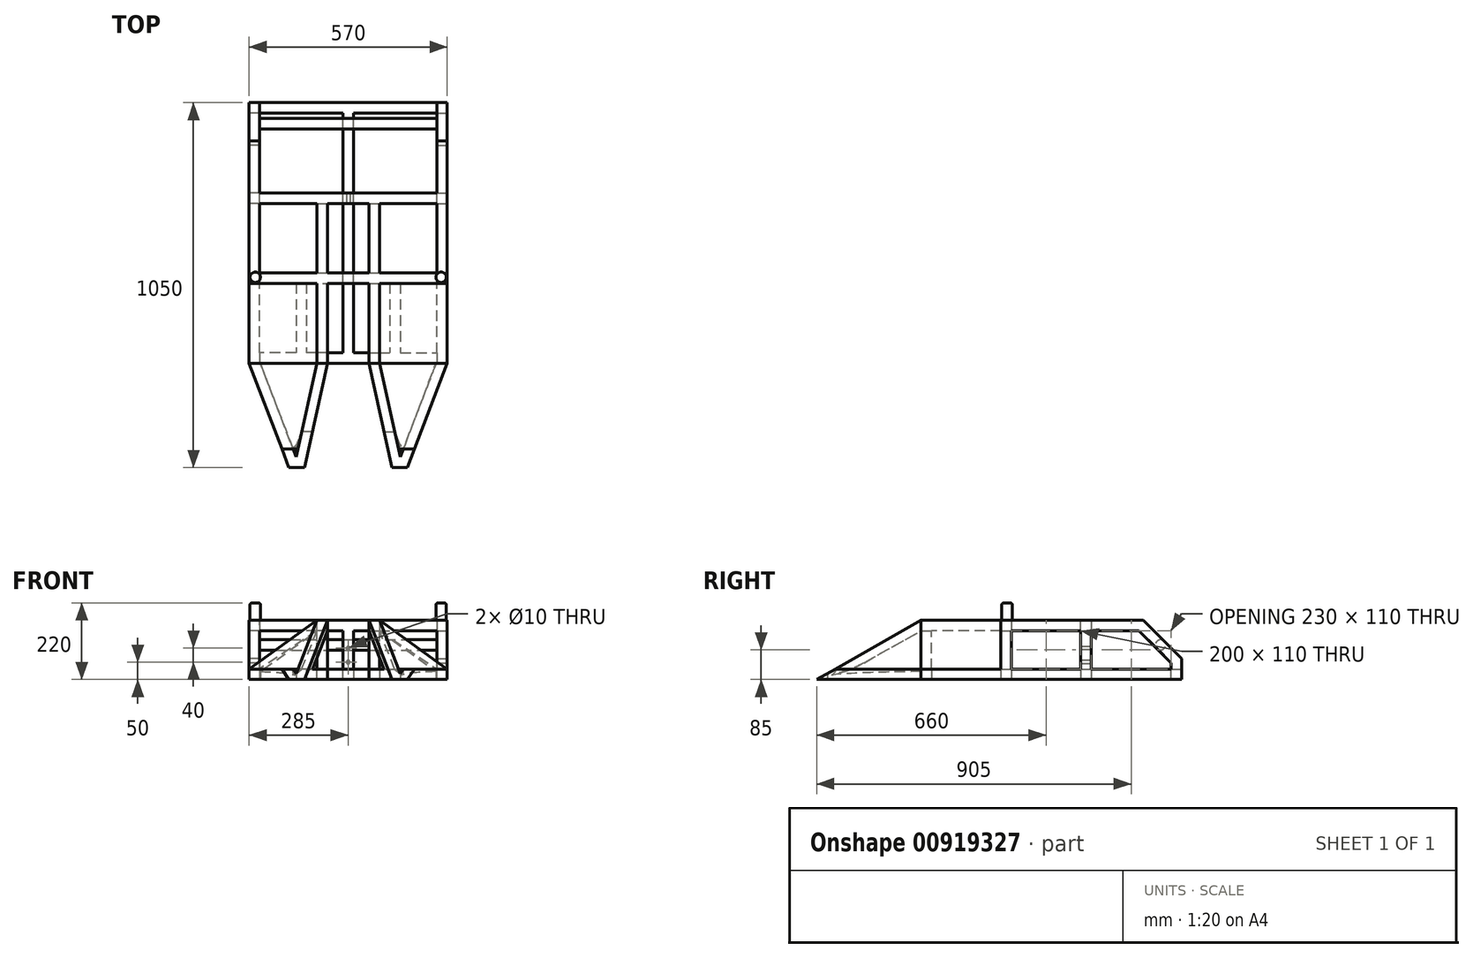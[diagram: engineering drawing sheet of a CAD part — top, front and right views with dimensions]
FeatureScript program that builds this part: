
annotation { "Feature Type Name" : "Feature", "Feature Type Description" : "" }
export const myFeature = defineFeature(function(context is Context, id is Id, definition is map)
    precondition{}
    {
        {
            var Q0;
            Q0=qCreatedBy(makeId("Front.planeOp"),FACE);
            var sketch = newSketch(context, id + "F0", { "sketchPlane" : qUnion([Q0])});
            skLineSegment(sketch, "E0.bottom", {"start": v(0, 0) * mm, "end": v(30, 0) * mm});
            skLineSegment(sketch, "E0.top", {"start": v(0, 30) * mm, "end": v(30, 30) * mm});
            skLineSegment(sketch, "E0.left", {"start": v(0, 0) * mm, "end": v(0, 30) * mm});
            skLineSegment(sketch, "E0.right", {"start": v(30, 0) * mm, "end": v(30, 30) * mm});
            skSolve(sketch);
        }
        {
            var Q0;
            Q0=makeQuery(id+"F0.imprint","IMPRINT",FACE,{"disambiguationData":[TD([[makeQuery(id+"F0.imprint","IMPRINT",EDGE,{"derivedFrom":sQuery(id+"F0.wireOp",EDGE,"E0.bottom")}),1.0]])]});
            extrude(context, id + "F1", {"entities" : qUnion([Q0]), "depth" : 750 * mm, "offsetDistance" : 25 * mm});
        }
        {
            var Q0;
            Q0=makeQuery(id+"F1.opExtrude","SWEPT_FACE",FACE,{"disambiguationData":[OSD([sQuery(id+"F0.wireOp",EDGE,"E0.right")])]});
            var sketch = newSketch(context, id + "F2", { "sketchPlane" : qUnion([Q0])});
            skLineSegment(sketch, "E1.bottom", {"start": v(-750, 0) * mm, "end": v(-720, 0) * mm});
            skLineSegment(sketch, "E1.top", {"start": v(-750, 30) * mm, "end": v(-720, 30) * mm});
            skLineSegment(sketch, "E1.left", {"start": v(-750, 0) * mm, "end": v(-750, 30) * mm});
            skLineSegment(sketch, "E1.right", {"start": v(-720, 0) * mm, "end": v(-720, 30) * mm});
            skLineSegment(sketch, "E2.bottom", {"start": v(0, 0) * mm, "end": v(-30, 0) * mm});
            skLineSegment(sketch, "E2.top", {"start": v(0, 30) * mm, "end": v(-30, 30) * mm});
            skLineSegment(sketch, "E2.left", {"start": v(0, 0) * mm, "end": v(0, 30) * mm});
            skLineSegment(sketch, "E2.right", {"start": v(-30, 0) * mm, "end": v(-30, 30) * mm});
            skLineSegment(sketch, "E3.bottom", {"start": v(-390, 0) * mm, "end": v(-360, 0) * mm});
            skLineSegment(sketch, "E3.top", {"start": v(-390, 30) * mm, "end": v(-360, 30) * mm});
            skLineSegment(sketch, "E3.left", {"start": v(-390, 0) * mm, "end": v(-390, 30) * mm});
            skLineSegment(sketch, "E3.right", {"start": v(-360, 0) * mm, "end": v(-360, 30) * mm});
            skSolve(sketch);
        }
        {
            var Q0;
            Q0 = qSketchRegion(id + "F2", true);
            extrude(context, id + "F3", {"entities" : qUnion([Q0]), "operationType" : NewBodyOperationType.ADD, "depth" : 120 * mm, "offsetDistance" : 25 * mm});
        }
        {
            var Q0;
            Q0=makeQuery(id+"F3.boolean.opBoolean","MERGE",FACE,{"derivedFrom":[makeQuery(id+"F1.opExtrude","SWEPT_FACE",FACE,{"disambiguationData":[OSD([sQuery(id+"F0.wireOp",EDGE,"E0.top")])]}),makeQuery(id+"F3.opExtrude","SWEPT_FACE",FACE,{"disambiguationData":[OSD([sQuery(id+"F2.wireOp",EDGE,"E1.top")])]}),makeQuery(id+"F3.opExtrude","SWEPT_FACE",FACE,{"disambiguationData":[OSD([sQuery(id+"F2.wireOp",EDGE,"E2.top")])]}),makeQuery(id+"F3.opExtrude","SWEPT_FACE",FACE,{"disambiguationData":[OSD([sQuery(id+"F2.wireOp",EDGE,"E3.top")])]})]});
            var sketch = newSketch(context, id + "F4", { "sketchPlane" : qUnion([Q0])});
            skLineSegment(sketch, "E4.bottom", {"start": v(0, -750) * mm, "end": v(30, -750) * mm});
            skLineSegment(sketch, "E4.top", {"start": v(0, -720) * mm, "end": v(30, -720) * mm});
            skLineSegment(sketch, "E4.left", {"start": v(0, -750) * mm, "end": v(0, -720) * mm});
            skLineSegment(sketch, "E4.right", {"start": v(30, -750) * mm, "end": v(30, -720) * mm});
            skLineSegment(sketch, "E5.bottom", {"start": v(30, -290) * mm, "end": v(0, -290) * mm});
            skLineSegment(sketch, "E5.top", {"start": v(30, -260) * mm, "end": v(0, -260) * mm});
            skLineSegment(sketch, "E5.left", {"start": v(30, -290) * mm, "end": v(30, -260) * mm});
            skLineSegment(sketch, "E5.right", {"start": v(0, -290) * mm, "end": v(0, -260) * mm});
            skLineSegment(sketch, "E6.bottom", {"start": v(0, -520) * mm, "end": v(30, -520) * mm});
            skLineSegment(sketch, "E6.top", {"start": v(0, -490) * mm, "end": v(30, -490) * mm});
            skLineSegment(sketch, "E6.left", {"start": v(0, -520) * mm, "end": v(0, -490) * mm});
            skLineSegment(sketch, "E6.right", {"start": v(30, -520) * mm, "end": v(30, -490) * mm});
            skSolve(sketch);
        }
        {
            var Q0;
            Q0 = qSketchRegion(id + "F4", true);
            extrude(context, id + "F5", {"entities" : qUnion([Q0]), "operationType" : NewBodyOperationType.ADD, "depth" : 140 * mm, "offsetDistance" : 25 * mm});
        }
        {
            var Q0;
            Q0=makeQuery(id+"F5.opExtrude","SWEPT_FACE",FACE,{"disambiguationData":[OSD([sQuery(id+"F4.wireOp",EDGE,"E4.top")])]});
            var sketch = newSketch(context, id + "F6", { "sketchPlane" : qUnion([Q0])});
            skLineSegment(sketch, "E7.bottom", {"start": v(-30, 170) * mm, "end": v(0, 170) * mm});
            skLineSegment(sketch, "E7.top", {"start": v(-30, 140) * mm, "end": v(0, 140) * mm});
            skLineSegment(sketch, "E7.left", {"start": v(-30, 170) * mm, "end": v(-30, 140) * mm});
            skLineSegment(sketch, "E7.right", {"start": v(0, 170) * mm, "end": v(0, 140) * mm});
            skSolve(sketch);
        }
        {
            var Q0;
            Q0=makeQuery(id+"F6.imprint","IMPRINT",FACE,{"disambiguationData":[TD([[makeQuery(id+"F6.imprint","IMPRINT",EDGE,{"derivedFrom":sQuery(id+"F6.wireOp",EDGE,"E7.bottom")}),1.0]])]});
            var Q1;
            Q1=makeQuery(id+"F5.opExtrude","SWEPT_FACE",FACE,{"disambiguationData":[OSD([sQuery(id+"F4.wireOp",EDGE,"E5.bottom")])]});
            extrude(context, id + "F7", {"entities" : qUnion([Q0]), "operationType" : NewBodyOperationType.ADD, "endBound" : BoundingType.UP_TO_SURFACE, "depth" : 25 * mm, "endBoundEntityFace" : qUnion([Q1]), "offsetDistance" : 25 * mm});
        }
        {
            var Q0;
            Q0=makeQuery(id+"F7.boolean.opBoolean","MERGE",FACE,{"derivedFrom":[makeQuery(id+"F5.boolean.opBoolean","MERGE",FACE,{"derivedFrom":[makeQuery(id+"F1.opExtrude","SWEPT_FACE",FACE,{"disambiguationData":[OSD([sQuery(id+"F0.wireOp",EDGE,"E0.left")])]}),makeQuery(id+"F5.opExtrude","SWEPT_FACE",FACE,{"disambiguationData":[OSD([sQuery(id+"F4.wireOp",EDGE,"E4.left")])]}),makeQuery(id+"F5.opExtrude","SWEPT_FACE",FACE,{"disambiguationData":[OSD([sQuery(id+"F4.wireOp",EDGE,"E5.right")])]}),makeQuery(id+"F5.opExtrude","SWEPT_FACE",FACE,{"disambiguationData":[OSD([sQuery(id+"F4.wireOp",EDGE,"E6.left")])]})]}),makeQuery(id+"F7.opExtrude","SWEPT_FACE",FACE,{"disambiguationData":[OSD([sQuery(id+"F6.wireOp",EDGE,"E7.right")])]})]});
            var sketch = newSketch(context, id + "F8", { "sketchPlane" : qUnion([Q0])});
            skArc(sketch, "E8", {"start": v(260, 170) * mm, "mid": v(112.35, 132.78) * mm, "end": v(0, 30) * mm});
            skArc(sketch, "E9", {"start": v(260, 140) * mm, "mid": v(133.23, 109.61) * mm, "end": v(30, 30) * mm});
            skLineSegment(sketch, "E10", {"start": v(0, 30) * mm, "end": v(30, 30) * mm});
            skLineSegment(sketch, "E11", {"start": v(260, 140) * mm, "end": v(260, 170) * mm});
            skSolve(sketch);
        }
        {
            var Q0;
            Q0=makeQuery(id+"F8.imprint","IMPRINT",FACE,{"disambiguationData":[TD([[makeQuery(id+"F8.imprint","IMPRINT",EDGE,{"derivedFrom":sQuery(id+"F8.wireOp",EDGE,"E8")}),1.0]])]});
            extrude(context, id + "F9", {"entities" : qUnion([Q0]), "operationType" : NewBodyOperationType.ADD, "oppositeDirection" : true, "depth" : 30 * mm, "offsetDistance" : 25 * mm});
        }
        {
            var Q0;
            {var subQ8=makeQuery(id+"F1.opExtrude","SWEPT_FACE",FACE,{"disambiguationData":[OSD([sQuery(id+"F0.wireOp",EDGE,"E0.right")])]});Q0=makeQuery(id+"F9.boolean.opBoolean","MERGE",FACE,{"derivedFrom":[makeQuery(id+"F7.boolean.opBoolean","MERGE",FACE,{"derivedFrom":[makeQuery(id+"F5.opExtrude","SWEPT_FACE",FACE,{"disambiguationData":[OSD([sQuery(id+"F4.wireOp",EDGE,"E4.right")])]}),makeQuery(id+"F5.boolean.opBoolean","MERGE",FACE,{"derivedFrom":[makeQuery(id+"F3.boolean.opBoolean","SPLIT",FACE,{"disambiguationData":[TD([makeQuery(id+"F3.opExtrude","SWEPT_FACE",FACE,{"disambiguationData":[OSD([sQuery(id+"F2.wireOp",EDGE,"E1.right")])]})])],"derivedFrom":subQ8}),makeQuery(id+"F5.opExtrude","SWEPT_FACE",FACE,{"disambiguationData":[OSD([sQuery(id+"F4.wireOp",EDGE,"E6.right")])]})]}),makeQuery(id+"F5.boolean.opBoolean","MERGE",FACE,{"derivedFrom":[makeQuery(id+"F3.boolean.opBoolean","SPLIT",FACE,{"disambiguationData":[TD([makeQuery(id+"F3.opExtrude","SWEPT_FACE",FACE,{"disambiguationData":[OSD([sQuery(id+"F2.wireOp",EDGE,"E2.right")])]})])],"derivedFrom":subQ8}),makeQuery(id+"F5.opExtrude","SWEPT_FACE",FACE,{"disambiguationData":[OSD([sQuery(id+"F4.wireOp",EDGE,"E5.left")])]})]}),makeQuery(id+"F7.opExtrude","SWEPT_FACE",FACE,{"disambiguationData":[OSD([sQuery(id+"F6.wireOp",EDGE,"E7.left")])]})]}),makeQuery(id+"F9.opExtrude","CAP_FACE",FACE,{"disambiguationData":[OSD([sQuery(id+"F8.wireOp",EDGE,"E8"),sQuery(id+"F8.wireOp",EDGE,"E9"),sQuery(id+"F8.wireOp",EDGE,"E10"),sQuery(id+"F8.wireOp",EDGE,"E11")])],"isStart":false})]});}
            var sketch = newSketch(context, id + "F10", { "sketchPlane" : qUnion([Q0])});
            skLineSegment(sketch, "E12.bottom", {"start": v(-750, 170) * mm, "end": v(-720, 170) * mm});
            skLineSegment(sketch, "E12.top", {"start": v(-750, 140) * mm, "end": v(-720, 140) * mm});
            skLineSegment(sketch, "E12.left", {"start": v(-750, 170) * mm, "end": v(-750, 140) * mm});
            skLineSegment(sketch, "E12.right", {"start": v(-720, 170) * mm, "end": v(-720, 140) * mm});
            skLineSegment(sketch, "E13.bottom", {"start": v(-520, 140) * mm, "end": v(-490, 140) * mm});
            skLineSegment(sketch, "E13.top", {"start": v(-520, 170) * mm, "end": v(-490, 170) * mm});
            skLineSegment(sketch, "E13.left", {"start": v(-520, 140) * mm, "end": v(-520, 170) * mm});
            skLineSegment(sketch, "E13.right", {"start": v(-490, 140) * mm, "end": v(-490, 170) * mm});
            skLineSegment(sketch, "E14.bottom", {"start": v(-290, 140) * mm, "end": v(-260, 140) * mm});
            skLineSegment(sketch, "E14.top", {"start": v(-290, 170) * mm, "end": v(-260, 170) * mm});
            skLineSegment(sketch, "E14.left", {"start": v(-290, 140) * mm, "end": v(-290, 170) * mm});
            skLineSegment(sketch, "E14.right", {"start": v(-260, 140) * mm, "end": v(-260, 170) * mm});
            skSolve(sketch);
        }
        {
            var Q0;
            Q0 = qSketchRegion(id + "F10", true);
            var Q1;
            Q1=makeQuery(id+"F3.opExtrude","CAP_FACE",FACE,{"disambiguationData":[OSD([sQuery(id+"F2.wireOp",EDGE,"E1.bottom"),sQuery(id+"F2.wireOp",EDGE,"E1.top"),sQuery(id+"F2.wireOp",EDGE,"E1.left"),sQuery(id+"F2.wireOp",EDGE,"E1.right")])],"isStart":false});
            extrude(context, id + "F11", {"entities" : qUnion([Q0]), "operationType" : NewBodyOperationType.ADD, "endBound" : BoundingType.UP_TO_SURFACE, "depth" : 25 * mm, "endBoundEntityFace" : qUnion([Q1]), "offsetDistance" : 25 * mm});
        }
        {
            var Q0;
            Q0=makeQuery(id+"F1.opExtrude","SWEPT_BODY",BODY,{"disambiguationData":[OSD([sQuery(id+"F0.wireOp",EDGE,"E0.bottom"),sQuery(id+"F0.wireOp",EDGE,"E0.top"),sQuery(id+"F0.wireOp",EDGE,"E0.left"),sQuery(id+"F0.wireOp",EDGE,"E0.right")])]});
            var Q1;
            Q1=makeQuery(id+"F3.opExtrude","CAP_FACE",FACE,{"disambiguationData":[OSD([sQuery(id+"F2.wireOp",EDGE,"E3.bottom"),sQuery(id+"F2.wireOp",EDGE,"E3.top"),sQuery(id+"F2.wireOp",EDGE,"E3.left"),sQuery(id+"F2.wireOp",EDGE,"E3.right")])],"isStart":false});
            mirror(context, id + "F12", {"operationType" : NewBodyOperationType.ADD, "entities" : qUnion([Q0]), "mirrorPlane" : qUnion([Q1])});
        }
        {
            var Q0;
            {var subQ0=makeQuery(id+"F11.boolean.opBoolean","MERGE",FACE,{"derivedFrom":[makeQuery(id+"F7.boolean.opBoolean","MERGE",FACE,{"derivedFrom":[makeQuery(id+"F5.opExtrude","CAP_FACE",FACE,{"disambiguationData":[OSD([sQuery(id+"F4.wireOp",EDGE,"E4.bottom"),sQuery(id+"F4.wireOp",EDGE,"E4.top"),sQuery(id+"F4.wireOp",EDGE,"E4.left"),sQuery(id+"F4.wireOp",EDGE,"E4.right")])],"isStart":false}),makeQuery(id+"F5.opExtrude","CAP_FACE",FACE,{"disambiguationData":[OSD([sQuery(id+"F4.wireOp",EDGE,"E5.bottom"),sQuery(id+"F4.wireOp",EDGE,"E5.top"),sQuery(id+"F4.wireOp",EDGE,"E5.left"),sQuery(id+"F4.wireOp",EDGE,"E5.right")])],"isStart":false}),makeQuery(id+"F5.opExtrude","CAP_FACE",FACE,{"disambiguationData":[OSD([sQuery(id+"F4.wireOp",EDGE,"E6.bottom"),sQuery(id+"F4.wireOp",EDGE,"E6.top"),sQuery(id+"F4.wireOp",EDGE,"E6.left"),sQuery(id+"F4.wireOp",EDGE,"E6.right")])],"isStart":false}),makeQuery(id+"F7.opExtrude","SWEPT_FACE",FACE,{"disambiguationData":[OSD([sQuery(id+"F6.wireOp",EDGE,"E7.bottom")])]})]}),makeQuery(id+"F11.opExtrude","SWEPT_FACE",FACE,{"disambiguationData":[OSD([sQuery(id+"F10.wireOp",EDGE,"E12.bottom")])]}),makeQuery(id+"F11.opExtrude","SWEPT_FACE",FACE,{"disambiguationData":[OSD([sQuery(id+"F10.wireOp",EDGE,"E13.top")])]}),makeQuery(id+"F11.opExtrude","SWEPT_FACE",FACE,{"disambiguationData":[OSD([sQuery(id+"F10.wireOp",EDGE,"E14.top")])]})]});Q0=makeQuery(id+"F12.boolean.opBoolean","MERGE",FACE,{"derivedFrom":[subQ0,makeQuery(id+"F12.opPattern","COPY",FACE,{"derivedFrom":subQ0,"instanceName":"1"})]});}
            var sketch = newSketch(context, id + "F13", { "sketchPlane" : qUnion([Q0])});
            skLineSegment(sketch, "E15.bottom", {"start": v(285, -750) * mm, "end": v(315, -750) * mm});
            skLineSegment(sketch, "E15.top", {"start": v(285, 0) * mm, "end": v(315, 0) * mm});
            skLineSegment(sketch, "E15.left", {"start": v(285, -750) * mm, "end": v(285, 0) * mm});
            skLineSegment(sketch, "E15.right", {"start": v(315, -750) * mm, "end": v(315, 0) * mm});
            skSolve(sketch);
        }
        {
            var Q0;
            Q0 = qSketchRegion(id + "F13", true);
            extrude(context, id + "F14", {"entities" : qUnion([Q0]), "operationType" : NewBodyOperationType.REMOVE, "endBound" : BoundingType.THROUGH_ALL, "oppositeDirection" : true, "depth" : 25 * mm, "offsetDistance" : 25 * mm});
        }
        {
            var Q0;
            Q0=makeQuery(id+"F1.opExtrude","SWEPT_BODY",BODY,{"disambiguationData":[OSD([sQuery(id+"F0.wireOp",EDGE,"E0.bottom"),sQuery(id+"F0.wireOp",EDGE,"E0.top"),sQuery(id+"F0.wireOp",EDGE,"E0.left"),sQuery(id+"F0.wireOp",EDGE,"E0.right")])]});
            var Q1;
            Q1=makeQuery(id+"F14.boolean.opBoolean","COPY",FACE,{"derivedFrom":makeQuery(id+"F14.opExtrude","SWEPT_FACE",FACE,{"disambiguationData":[OSD([sQuery(id+"F13.wireOp",EDGE,"E15.left")])]})});
            mirror(context, id + "F15", {"operationType" : NewBodyOperationType.ADD, "entities" : qUnion([Q0]), "mirrorPlane" : qUnion([Q1])});
        }
        {
            var Q0;
            {var subQ0=makeQuery(id+"F11.boolean.opBoolean","MERGE",FACE,{"derivedFrom":[makeQuery(id+"F7.boolean.opBoolean","MERGE",FACE,{"derivedFrom":[makeQuery(id+"F5.opExtrude","CAP_FACE",FACE,{"disambiguationData":[OSD([sQuery(id+"F4.wireOp",EDGE,"E4.bottom"),sQuery(id+"F4.wireOp",EDGE,"E4.top"),sQuery(id+"F4.wireOp",EDGE,"E4.left"),sQuery(id+"F4.wireOp",EDGE,"E4.right")])],"isStart":false}),makeQuery(id+"F5.opExtrude","CAP_FACE",FACE,{"disambiguationData":[OSD([sQuery(id+"F4.wireOp",EDGE,"E5.bottom"),sQuery(id+"F4.wireOp",EDGE,"E5.top"),sQuery(id+"F4.wireOp",EDGE,"E5.left"),sQuery(id+"F4.wireOp",EDGE,"E5.right")])],"isStart":false}),makeQuery(id+"F5.opExtrude","CAP_FACE",FACE,{"disambiguationData":[OSD([sQuery(id+"F4.wireOp",EDGE,"E6.bottom"),sQuery(id+"F4.wireOp",EDGE,"E6.top"),sQuery(id+"F4.wireOp",EDGE,"E6.left"),sQuery(id+"F4.wireOp",EDGE,"E6.right")])],"isStart":false}),makeQuery(id+"F7.opExtrude","SWEPT_FACE",FACE,{"disambiguationData":[OSD([sQuery(id+"F6.wireOp",EDGE,"E7.bottom")])]})]}),makeQuery(id+"F11.opExtrude","SWEPT_FACE",FACE,{"disambiguationData":[OSD([sQuery(id+"F10.wireOp",EDGE,"E12.bottom")])]}),makeQuery(id+"F11.opExtrude","SWEPT_FACE",FACE,{"disambiguationData":[OSD([sQuery(id+"F10.wireOp",EDGE,"E13.top")])]}),makeQuery(id+"F11.opExtrude","SWEPT_FACE",FACE,{"disambiguationData":[OSD([sQuery(id+"F10.wireOp",EDGE,"E14.top")])]})]});var subQ1=makeQuery(id+"F12.boolean.opBoolean","MERGE",FACE,{"derivedFrom":[subQ0,makeQuery(id+"F12.opPattern","COPY",FACE,{"derivedFrom":subQ0,"instanceName":"1"})]});Q0=makeQuery(id+"F15.boolean.opBoolean","MERGE",FACE,{"derivedFrom":[subQ1,makeQuery(id+"F15.opPattern","COPY",FACE,{"derivedFrom":subQ1,"instanceName":"1"})]});}
            var sketch = newSketch(context, id + "F16", { "sketchPlane" : qUnion([Q0])});
            skLineSegment(sketch, "E16.bottom", {"start": v(345, -520) * mm, "end": v(225, -520) * mm});
            skLineSegment(sketch, "E16.top", {"start": v(225, -750) * mm, "end": v(345, -750) * mm});
            skLineSegment(sketch, "E16.left", {"start": v(225, -520) * mm, "end": v(225, -750) * mm});
            skLineSegment(sketch, "E16.right", {"start": v(345, -520) * mm, "end": v(345, -750) * mm});
            skSolve(sketch);
        }
        {
            var Q0;
            Q0 = qSketchRegion(id + "F16", true);
            var Q1;
            {var subQ0=makeQuery(id+"F3.opExtrude","SWEPT_FACE",FACE,{"disambiguationData":[OSD([sQuery(id+"F2.wireOp",EDGE,"E2.top")])]});var subQ2=sQuery(id+"F2.wireOp",EDGE,"E1.top");var subQ3=makeQuery(id+"F3.opExtrude","SWEPT_FACE",FACE,{"disambiguationData":[OSD([subQ2])]});var subQ5=sQuery(id+"F0.wireOp",EDGE,"E0.top");var subQ6=makeQuery(id+"F3.opExtrude","SWEPT_FACE",FACE,{"disambiguationData":[OSD([sQuery(id+"F2.wireOp",EDGE,"E3.top")])]});var subQ7=sQuery(id+"F2.wireOp",EDGE,"E1.left");var subQ8=makeQuery(id+"F1.opExtrude","SWEPT_FACE",FACE,{"disambiguationData":[OSD([subQ5])]});var subQ9=makeQuery(id+"F5.boolean.opBoolean","SPLIT",FACE,{"disambiguationData":[TD([makeQuery(id+"F3.opExtrude","SWEPT_FACE",FACE,{"disambiguationData":[OSD([subQ7])]})])],"derivedFrom":makeQuery(id+"F3.boolean.opBoolean","MERGE",FACE,{"derivedFrom":[subQ8,subQ3,subQ0,subQ6]})});Q1=makeQuery(id+"F12.boolean.opBoolean","MERGE",FACE,{"derivedFrom":[subQ9,makeQuery(id+"F12.opPattern","COPY",FACE,{"derivedFrom":subQ9,"instanceName":"1"})]});}
            extrude(context, id + "F17", {"entities" : qUnion([Q0]), "operationType" : NewBodyOperationType.REMOVE, "endBound" : BoundingType.UP_TO_SURFACE, "oppositeDirection" : true, "depth" : 30 * mm, "endBoundEntityFace" : qUnion([Q1]), "offsetDistance" : 25 * mm});
        }
        {
            var Q0;
            {var subQ0=makeQuery(id+"F11.boolean.opBoolean","MERGE",FACE,{"derivedFrom":[makeQuery(id+"F7.boolean.opBoolean","MERGE",FACE,{"derivedFrom":[makeQuery(id+"F5.opExtrude","CAP_FACE",FACE,{"disambiguationData":[OSD([sQuery(id+"F4.wireOp",EDGE,"E4.bottom"),sQuery(id+"F4.wireOp",EDGE,"E4.top"),sQuery(id+"F4.wireOp",EDGE,"E4.left"),sQuery(id+"F4.wireOp",EDGE,"E4.right")])],"isStart":false}),makeQuery(id+"F5.opExtrude","CAP_FACE",FACE,{"disambiguationData":[OSD([sQuery(id+"F4.wireOp",EDGE,"E5.bottom"),sQuery(id+"F4.wireOp",EDGE,"E5.top"),sQuery(id+"F4.wireOp",EDGE,"E5.left"),sQuery(id+"F4.wireOp",EDGE,"E5.right")])],"isStart":false}),makeQuery(id+"F5.opExtrude","CAP_FACE",FACE,{"disambiguationData":[OSD([sQuery(id+"F4.wireOp",EDGE,"E6.bottom"),sQuery(id+"F4.wireOp",EDGE,"E6.top"),sQuery(id+"F4.wireOp",EDGE,"E6.left"),sQuery(id+"F4.wireOp",EDGE,"E6.right")])],"isStart":false}),makeQuery(id+"F7.opExtrude","SWEPT_FACE",FACE,{"disambiguationData":[OSD([sQuery(id+"F6.wireOp",EDGE,"E7.bottom")])]})]}),makeQuery(id+"F11.opExtrude","SWEPT_FACE",FACE,{"disambiguationData":[OSD([sQuery(id+"F10.wireOp",EDGE,"E12.bottom")])]}),makeQuery(id+"F11.opExtrude","SWEPT_FACE",FACE,{"disambiguationData":[OSD([sQuery(id+"F10.wireOp",EDGE,"E13.top")])]}),makeQuery(id+"F11.opExtrude","SWEPT_FACE",FACE,{"disambiguationData":[OSD([sQuery(id+"F10.wireOp",EDGE,"E14.top")])]})]});var subQ1=makeQuery(id+"F12.boolean.opBoolean","MERGE",FACE,{"derivedFrom":[subQ0,makeQuery(id+"F12.opPattern","COPY",FACE,{"derivedFrom":subQ0,"instanceName":"1"})]});Q0=makeQuery(id+"F15.boolean.opBoolean","MERGE",FACE,{"derivedFrom":[subQ1,makeQuery(id+"F15.opPattern","COPY",FACE,{"derivedFrom":subQ1,"instanceName":"1"})]});}
            var sketch = newSketch(context, id + "F18", { "sketchPlane" : qUnion([Q0])});
            skLineSegment(sketch, "E17.bottom", {"start": v(225, -720) * mm, "end": v(195, -720) * mm});
            skLineSegment(sketch, "E17.top", {"start": v(225, -520) * mm, "end": v(195, -520) * mm});
            skLineSegment(sketch, "E17.left", {"start": v(225, -720) * mm, "end": v(225, -520) * mm});
            skLineSegment(sketch, "E17.right", {"start": v(195, -720) * mm, "end": v(195, -520) * mm});
            skLineSegment(sketch, "E18.bottom", {"start": v(345, -720) * mm, "end": v(375, -720) * mm});
            skLineSegment(sketch, "E18.top", {"start": v(345, -520) * mm, "end": v(375, -520) * mm});
            skLineSegment(sketch, "E18.left", {"start": v(345, -720) * mm, "end": v(345, -520) * mm});
            skLineSegment(sketch, "E18.right", {"start": v(375, -720) * mm, "end": v(375, -520) * mm});
            skSolve(sketch);
        }
        {
            var Q0;
            Q0 = qSketchRegion(id + "F18", true);
            extrude(context, id + "F19", {"entities" : qUnion([Q0]), "operationType" : NewBodyOperationType.ADD, "oppositeDirection" : true, "depth" : 30 * mm, "offsetDistance" : 25 * mm});
        }
        {
            var Q0;
            {var subQ0=makeQuery(id+"F11.boolean.opBoolean","MERGE",FACE,{"derivedFrom":[makeQuery(id+"F5.boolean.opBoolean","MERGE",FACE,{"derivedFrom":[makeQuery(id+"F3.boolean.opBoolean","MERGE",FACE,{"derivedFrom":[makeQuery(id+"F1.opExtrude","CAP_FACE",FACE,{"disambiguationData":[OSD([sQuery(id+"F0.wireOp",EDGE,"E0.bottom"),sQuery(id+"F0.wireOp",EDGE,"E0.top"),sQuery(id+"F0.wireOp",EDGE,"E0.left"),sQuery(id+"F0.wireOp",EDGE,"E0.right")])],"isStart":false}),makeQuery(id+"F3.opExtrude","SWEPT_FACE",FACE,{"disambiguationData":[OSD([sQuery(id+"F2.wireOp",EDGE,"E1.left")])]})]}),makeQuery(id+"F5.opExtrude","SWEPT_FACE",FACE,{"disambiguationData":[OSD([sQuery(id+"F4.wireOp",EDGE,"E4.bottom")])]})]}),makeQuery(id+"F11.opExtrude","SWEPT_FACE",FACE,{"disambiguationData":[OSD([sQuery(id+"F10.wireOp",EDGE,"E12.left")])]})]});var subQ1=makeQuery(id+"F12.boolean.opBoolean","MERGE",FACE,{"derivedFrom":[subQ0,makeQuery(id+"F12.opPattern","COPY",FACE,{"derivedFrom":subQ0,"instanceName":"1"})]});Q0=makeQuery(id+"F15.boolean.opBoolean","MERGE",FACE,{"derivedFrom":[subQ1,makeQuery(id+"F15.opPattern","COPY",FACE,{"derivedFrom":subQ1,"instanceName":"1"})]});}
            var sketch = newSketch(context, id + "F20", { "sketchPlane" : qUnion([Q0])});
            skLineSegment(sketch, "E19", {"start": v(0, 30) * mm, "end": v(0, 170) * mm});
            skLineSegment(sketch, "E20", {"start": v(0, 170) * mm, "end": v(195, 170) * mm});
            skLineSegment(sketch, "E21", {"start": v(195, 170) * mm, "end": v(195, 140) * mm});
            skLineSegment(sketch, "E22", {"start": v(195, 140) * mm, "end": v(375, 140) * mm});
            skLineSegment(sketch, "E23", {"start": v(375, 140) * mm, "end": v(375, 170) * mm});
            skLineSegment(sketch, "E24", {"start": v(375, 170) * mm, "end": v(570, 170) * mm});
            skLineSegment(sketch, "E25", {"start": v(570, 170) * mm, "end": v(570, 30) * mm});
            skLineSegment(sketch, "E26", {"start": v(570, 30) * mm, "end": v(0, 30) * mm});
            skSolve(sketch);
        }
        {
            var Q0;
            {var subQ10=sQuery(id+"F20.wireOp",EDGE,"E23");Q0=makeQuery(id+"F20.imprint","IMPRINT",FACE,{"disambiguationData":[TD([[makeQuery(id+"F20.imprint","IMPRINT",EDGE,{"derivedFrom":subQ10}),-1.0]])]});}
            var Q1;
            {var subQ8=sQuery(id+"F20.wireOp",EDGE,"E19");Q1=makeQuery(id+"F20.imprint","IMPRINT",FACE,{"disambiguationData":[TD([[makeQuery(id+"F20.imprint","IMPRINT",EDGE,{"derivedFrom":subQ8}),-1.0]])]});}
            var Q2;
            {var subQ9=sQuery(id+"F4.wireOp",EDGE,"E6.bottom");var subQ19=makeQuery(id+"F5.opExtrude","SWEPT_FACE",FACE,{"disambiguationData":[OSD([subQ9])]});var subQ20=makeQuery(id+"F12.opPattern","COPY",FACE,{"derivedFrom":subQ19,"instanceName":"1"});var subQ21=makeQuery(id+"F11.opExtrude","SWEPT_FACE",FACE,{"disambiguationData":[OSD([sQuery(id+"F10.wireOp",EDGE,"E13.left")])]});var subQ22=makeQuery(id+"F12.boolean.opBoolean","MERGE",FACE,{"derivedFrom":[subQ21,makeQuery(id+"F12.opPattern","COPY",FACE,{"derivedFrom":subQ21,"instanceName":"1"})]});Q2=makeQuery(id+"F19.boolean.opBoolean","SPLIT",FACE,{"disambiguationData":[TD([makeQuery(id+"F1.opExtrude","SWEPT_FACE",FACE,{"disambiguationData":[OSD([sQuery(id+"F0.wireOp",EDGE,"E0.right")])]})])],"derivedFrom":makeQuery(id+"F17.boolean.opBoolean","MERGE",FACE,{"derivedFrom":[subQ22,makeQuery(id+"F15.opPattern","COPY",FACE,{"derivedFrom":subQ22,"instanceName":"1"}),makeQuery(id+"F15.boolean.opBoolean","MERGE",FACE,{"derivedFrom":[subQ20,makeQuery(id+"F15.opPattern","COPY",FACE,{"derivedFrom":subQ20,"instanceName":"1"})]})],"fromTools":[makeQuery(id+"F17.opExtrude","SWEPT_FACE",FACE,{"disambiguationData":[OSD([sQuery(id+"F16.wireOp",EDGE,"E16.bottom")])]})]})});}
            extrude(context, id + "F21", {"entities" : qUnion([Q0, Q1]), "operationType" : NewBodyOperationType.REMOVE, "endBound" : BoundingType.UP_TO_SURFACE, "oppositeDirection" : true, "depth" : 25 * mm, "endBoundEntityFace" : qUnion([Q2]), "offsetDistance" : 25 * mm});
        }
        {
            var Q0;
            {var subQ0=makeQuery(id+"F3.boolean.opBoolean","MERGE",FACE,{"derivedFrom":[makeQuery(id+"F1.opExtrude","SWEPT_FACE",FACE,{"disambiguationData":[OSD([sQuery(id+"F0.wireOp",EDGE,"E0.bottom")])]}),makeQuery(id+"F3.opExtrude","SWEPT_FACE",FACE,{"disambiguationData":[OSD([sQuery(id+"F2.wireOp",EDGE,"E1.bottom")])]}),makeQuery(id+"F3.opExtrude","SWEPT_FACE",FACE,{"disambiguationData":[OSD([sQuery(id+"F2.wireOp",EDGE,"E2.bottom")])]}),makeQuery(id+"F3.opExtrude","SWEPT_FACE",FACE,{"disambiguationData":[OSD([sQuery(id+"F2.wireOp",EDGE,"E3.bottom")])]})]});var subQ1=makeQuery(id+"F12.boolean.opBoolean","MERGE",FACE,{"derivedFrom":[subQ0,makeQuery(id+"F12.opPattern","COPY",FACE,{"derivedFrom":subQ0,"instanceName":"1"})]});Q0=makeQuery(id+"F15.boolean.opBoolean","MERGE",FACE,{"derivedFrom":[subQ1,makeQuery(id+"F15.opPattern","COPY",FACE,{"derivedFrom":subQ1,"instanceName":"1"})]});}
            var sketch = newSketch(context, id + "F22", { "sketchPlane" : qUnion([Q0])});
            skLineSegment(sketch, "E27", {"start": v(0, 750) * mm, "end": v(114.33, 1050) * mm});
            skLineSegment(sketch, "E28", {"start": v(114.33, 1050) * mm, "end": v(159.13, 1050) * mm});
            skLineSegment(sketch, "E29", {"start": v(159.13, 1050) * mm, "end": v(225, 750) * mm});
            skLineSegment(sketch, "E30", {"start": v(225, 750) * mm, "end": v(194.29, 750) * mm});
            skLineSegment(sketch, "E31", {"start": v(194.29, 750) * mm, "end": v(135, 1020) * mm});
            skLineSegment(sketch, "E32", {"start": v(135, 1020) * mm, "end": v(135, 1020) * mm});
            skLineSegment(sketch, "E33", {"start": v(135, 1020) * mm, "end": v(32.1, 750) * mm});
            skLineSegment(sketch, "E34", {"start": v(32.1, 750) * mm, "end": v(0, 750) * mm});
            skLineSegment(sketch, "E35", {"start": v(570, 750) * mm, "end": v(455.67, 1050) * mm});
            skLineSegment(sketch, "E36", {"start": v(455.67, 1050) * mm, "end": v(410.87, 1050) * mm});
            skLineSegment(sketch, "E37", {"start": v(410.87, 1050) * mm, "end": v(345, 750) * mm});
            skLineSegment(sketch, "E38", {"start": v(345, 750) * mm, "end": v(375.71, 750) * mm});
            skLineSegment(sketch, "E39", {"start": v(375.71, 750) * mm, "end": v(435, 1020) * mm});
            skLineSegment(sketch, "E40", {"start": v(435, 1020) * mm, "end": v(435, 1020) * mm});
            skLineSegment(sketch, "E41", {"start": v(435, 1020) * mm, "end": v(537.9, 750) * mm});
            skLineSegment(sketch, "E42", {"start": v(537.9, 750) * mm, "end": v(570, 750) * mm});
            skSolve(sketch);
        }
        {
            var Q0;
            Q0=makeQuery(id+"F22.imprint","IMPRINT",FACE,{"disambiguationData":[TD([[makeQuery(id+"F22.imprint","IMPRINT",EDGE,{"derivedFrom":sQuery(id+"F22.wireOp",EDGE,"E27")}),-1.0]])]});
            var Q1;
            Q1=makeQuery(id+"F22.imprint","IMPRINT",FACE,{"disambiguationData":[TD([[makeQuery(id+"F22.imprint","IMPRINT",EDGE,{"derivedFrom":sQuery(id+"F22.wireOp",EDGE,"E35")}),1.0]])]});
            extrude(context, id + "F23", {"entities" : qUnion([Q0, Q1]), "operationType" : NewBodyOperationType.ADD, "oppositeDirection" : true, "depth" : 30 * mm, "offsetDistance" : 25 * mm});
        }
        {
            var Q0;
            Q0=makeQuery(id+"F9.boolean.opBoolean","MERGE",FACE,{"derivedFrom":[makeQuery(id+"F7.boolean.opBoolean","MERGE",FACE,{"derivedFrom":[makeQuery(id+"F5.boolean.opBoolean","MERGE",FACE,{"derivedFrom":[makeQuery(id+"F1.opExtrude","SWEPT_FACE",FACE,{"disambiguationData":[OSD([sQuery(id+"F0.wireOp",EDGE,"E0.left")])]}),makeQuery(id+"F5.opExtrude","SWEPT_FACE",FACE,{"disambiguationData":[OSD([sQuery(id+"F4.wireOp",EDGE,"E4.left")])]}),makeQuery(id+"F5.opExtrude","SWEPT_FACE",FACE,{"disambiguationData":[OSD([sQuery(id+"F4.wireOp",EDGE,"E5.right")])]}),makeQuery(id+"F5.opExtrude","SWEPT_FACE",FACE,{"disambiguationData":[OSD([sQuery(id+"F4.wireOp",EDGE,"E6.left")])]})]}),makeQuery(id+"F7.opExtrude","SWEPT_FACE",FACE,{"disambiguationData":[OSD([sQuery(id+"F6.wireOp",EDGE,"E7.right")])]})]}),makeQuery(id+"F9.opExtrude","CAP_FACE",FACE,{"disambiguationData":[OSD([sQuery(id+"F8.wireOp",EDGE,"E8"),sQuery(id+"F8.wireOp",EDGE,"E9"),sQuery(id+"F8.wireOp",EDGE,"E10"),sQuery(id+"F8.wireOp",EDGE,"E11")])],"isStart":true})]});
            var sketch = newSketch(context, id + "F24", { "sketchPlane" : qUnion([Q0])});
            skLineSegment(sketch, "E43", {"start": v(1050, 0) * mm, "end": v(750, 170) * mm});
            skLineSegment(sketch, "E44", {"start": v(1050, 0) * mm, "end": v(1050, 105.72) * mm});
            skLineSegment(sketch, "E45", {"start": v(1050, 105.72) * mm, "end": v(750, 170) * mm});
            skSolve(sketch);
        }
        {
            var Q0;
            {var subQ0=sQuery(id+"F24.wireOp",EDGE,"E44");Q0=makeQuery(id+"F24.imprint","IMPRINT",FACE,{"disambiguationData":[TD([[makeQuery(id+"F24.imprint","IMPRINT",EDGE,{"derivedFrom":subQ0}),1.0]])]});}
            extrude(context, id + "F25", {"entities" : qUnion([Q0]), "operationType" : NewBodyOperationType.REMOVE, "endBound" : BoundingType.THROUGH_ALL, "oppositeDirection" : true, "depth" : 25 * mm, "offsetDistance" : 25 * mm});
        }
        {
            var Q0;
            {var subQ0=sQuery(id+"F20.wireOp",EDGE,"E26");var subQ1=sQuery(id+"F4.wireOp",EDGE,"E4.right");var subQ2=sQuery(id+"F4.wireOp",EDGE,"E4.bottom");var subQ3=sQuery(id+"F2.wireOp",EDGE,"E1.left");var subQ4=sQuery(id+"F2.wireOp",EDGE,"E1.top");var subQ5=sQuery(id+"F0.wireOp",EDGE,"E0.top");var subQ6=makeQuery(id+"F5.opExtrude","SWEPT_EDGE",EDGE,{"disambiguationData":[OSD([subQ5,subQ4,subQ3,subQ2,subQ1])]});var subQ7=sQuery(id+"F4.wireOp",EDGE,"E4.left");var subQ8=sQuery(id+"F0.wireOp",EDGE,"E0.left");var subQ9=makeQuery(id+"F5.boolean.opBoolean","MERGE",EDGE,{"derivedFrom":[makeQuery(id+"F1.opExtrude","CAP_EDGE",EDGE,{"disambiguationData":[OSD([subQ8])],"isStart":false}),makeQuery(id+"F5.opExtrude","SWEPT_EDGE",EDGE,{"disambiguationData":[OSD([subQ2,subQ7])]})]});var subQ12=makeQuery(id+"F3.opExtrude","SWEPT_FACE",FACE,{"disambiguationData":[OSD([sQuery(id+"F2.wireOp",EDGE,"E2.top")])]});var subQ15=makeQuery(id+"F1.opExtrude","SWEPT_FACE",FACE,{"disambiguationData":[OSD([subQ5])]});var subQ16=makeQuery(id+"F3.opExtrude","SWEPT_FACE",FACE,{"disambiguationData":[OSD([sQuery(id+"F2.wireOp",EDGE,"E3.top")])]});var subQ19=makeQuery(id+"F3.opExtrude","SWEPT_FACE",FACE,{"disambiguationData":[OSD([subQ4])]});var subQ21=makeQuery(id+"F3.boolean.opBoolean","MERGE",FACE,{"derivedFrom":[subQ15,subQ19,subQ12,subQ16]});var subQ22=makeQuery(id+"F5.boolean.opBoolean","SPLIT",FACE,{"disambiguationData":[TD([makeQuery(id+"F5.opExtrude","SWEPT_FACE",FACE,{"disambiguationData":[OSD([sQuery(id+"F4.wireOp",EDGE,"E6.bottom")])]})])],"derivedFrom":subQ21});var subQ23=makeQuery(id+"F12.opPattern","COPY",FACE,{"derivedFrom":subQ22,"instanceName":"1"});var subQ24=makeQuery(id+"F5.boolean.opBoolean","SPLIT",FACE,{"disambiguationData":[TD([makeQuery(id+"F3.opExtrude","SWEPT_FACE",FACE,{"disambiguationData":[OSD([subQ3])]})])],"derivedFrom":subQ21});var subQ25=makeQuery(id+"F12.boolean.opBoolean","MERGE",FACE,{"derivedFrom":[subQ24,makeQuery(id+"F12.opPattern","COPY",FACE,{"derivedFrom":subQ24,"instanceName":"1"})]});Q0=makeQuery(id+"F23.boolean.opBoolean","MERGE",FACE,{"derivedFrom":[makeQuery(id+"F21.boolean.opBoolean","MERGE",FACE,{"derivedFrom":[subQ22,makeQuery(id+"F15.opPattern","COPY",FACE,{"derivedFrom":subQ22,"instanceName":"1"}),makeQuery(id+"F17.boolean.opBoolean","MERGE",FACE,{"derivedFrom":[subQ25,makeQuery(id+"F15.opPattern","COPY",FACE,{"derivedFrom":subQ25,"instanceName":"1"}),makeQuery(id+"F15.boolean.opBoolean","MERGE",FACE,{"derivedFrom":[subQ23,makeQuery(id+"F15.opPattern","COPY",FACE,{"derivedFrom":subQ23,"instanceName":"1"})]})],"fromTools":[makeQuery(id+"F17.opExtrude","CAP_FACE",FACE,{"disambiguationData":[OSD([sQuery(id+"F16.wireOp",EDGE,"E16.bottom"),sQuery(id+"F16.wireOp",EDGE,"E16.top"),sQuery(id+"F16.wireOp",EDGE,"E16.left"),sQuery(id+"F16.wireOp",EDGE,"E16.right")])],"isStart":false})]})],"fromTools":[makeQuery(id+"F21.opExtrude","SWEPT_FACE",FACE,{"disambiguationData":[OSD([subQ0]),TDD([makeQuery(id+"F20.imprint","IMPRINT",EDGE,{"disambiguationData":[TD([[makeQuery(id+"F20.imprint","INTERSECT",VERTEX,{"derivedFrom":[makeQuery(id+"F15.opPattern","COPY",EDGE,{"derivedFrom":subQ6,"instanceName":"1"}),subQ0]}),1.0],[makeQuery(id+"F20.imprint","INTERSECT",VERTEX,{"derivedFrom":[makeQuery(id+"F15.opPattern","COPY",EDGE,{"derivedFrom":subQ9,"instanceName":"1"}),sQuery(id+"F20.wireOp",EDGE,"E25"),subQ0]}),-1.0]])],"derivedFrom":subQ0})])]}),makeQuery(id+"F21.opExtrude","SWEPT_FACE",FACE,{"disambiguationData":[OSD([subQ0]),TDD([makeQuery(id+"F20.imprint","IMPRINT",EDGE,{"disambiguationData":[TD([[makeQuery(id+"F20.imprint","INTERSECT",VERTEX,{"derivedFrom":[subQ6,subQ0]}),-1.0],[makeQuery(id+"F20.imprint","INTERSECT",VERTEX,{"derivedFrom":[subQ9,sQuery(id+"F20.wireOp",EDGE,"E19"),subQ0]}),1.0]])],"derivedFrom":subQ0})])]})]}),makeQuery(id+"F23.opExtrude","CAP_FACE",FACE,{"disambiguationData":[OSD([sQuery(id+"F22.wireOp",EDGE,"E27"),sQuery(id+"F22.wireOp",EDGE,"E28"),sQuery(id+"F22.wireOp",EDGE,"E29"),sQuery(id+"F22.wireOp",EDGE,"E30"),sQuery(id+"F22.wireOp",EDGE,"E31"),sQuery(id+"F22.wireOp",EDGE,"E32"),sQuery(id+"F22.wireOp",EDGE,"E33"),sQuery(id+"F22.wireOp",EDGE,"E34")])],"isStart":false}),makeQuery(id+"F23.opExtrude","CAP_FACE",FACE,{"disambiguationData":[OSD([sQuery(id+"F22.wireOp",EDGE,"E35"),sQuery(id+"F22.wireOp",EDGE,"E36"),sQuery(id+"F22.wireOp",EDGE,"E37"),sQuery(id+"F22.wireOp",EDGE,"E38"),sQuery(id+"F22.wireOp",EDGE,"E39"),sQuery(id+"F22.wireOp",EDGE,"E40"),sQuery(id+"F22.wireOp",EDGE,"E41"),sQuery(id+"F22.wireOp",EDGE,"E42")])],"isStart":false})]});}
            var sketch = newSketch(context, id + "F26", { "sketchPlane" : qUnion([Q0])});
            skLineSegment(sketch, "E46", {"start": v(285, -1038.53) * mm, "end": v(285, -783.22) * mm, "construction": true});
            skLineSegment(sketch, "E47.bottom", {"start": v(540, -720) * mm, "end": v(570, -720) * mm});
            skLineSegment(sketch, "E47.top", {"start": v(540, -750) * mm, "end": v(570, -750) * mm});
            skLineSegment(sketch, "E47.left", {"start": v(540, -720) * mm, "end": v(540, -750) * mm});
            skLineSegment(sketch, "E47.right", {"start": v(570, -720) * mm, "end": v(570, -750) * mm});
            skSolve(sketch);
        }
        {
            var Q0;
            {var subQ0=sQuery(id+"F20.wireOp",EDGE,"E26");var subQ1=sQuery(id+"F4.wireOp",EDGE,"E4.right");var subQ2=sQuery(id+"F4.wireOp",EDGE,"E4.bottom");var subQ3=sQuery(id+"F2.wireOp",EDGE,"E1.left");var subQ4=sQuery(id+"F2.wireOp",EDGE,"E1.top");var subQ5=sQuery(id+"F0.wireOp",EDGE,"E0.top");var subQ6=makeQuery(id+"F5.opExtrude","SWEPT_EDGE",EDGE,{"disambiguationData":[OSD([subQ5,subQ4,subQ3,subQ2,subQ1])]});var subQ7=sQuery(id+"F4.wireOp",EDGE,"E4.left");var subQ8=sQuery(id+"F0.wireOp",EDGE,"E0.left");var subQ9=makeQuery(id+"F5.boolean.opBoolean","MERGE",EDGE,{"derivedFrom":[makeQuery(id+"F1.opExtrude","CAP_EDGE",EDGE,{"disambiguationData":[OSD([subQ8])],"isStart":false}),makeQuery(id+"F5.opExtrude","SWEPT_EDGE",EDGE,{"disambiguationData":[OSD([subQ2,subQ7])]})]});var subQ12=makeQuery(id+"F3.opExtrude","SWEPT_FACE",FACE,{"disambiguationData":[OSD([sQuery(id+"F2.wireOp",EDGE,"E2.top")])]});var subQ15=makeQuery(id+"F1.opExtrude","SWEPT_FACE",FACE,{"disambiguationData":[OSD([subQ5])]});var subQ16=makeQuery(id+"F3.opExtrude","SWEPT_FACE",FACE,{"disambiguationData":[OSD([sQuery(id+"F2.wireOp",EDGE,"E3.top")])]});var subQ19=makeQuery(id+"F3.opExtrude","SWEPT_FACE",FACE,{"disambiguationData":[OSD([subQ4])]});var subQ21=makeQuery(id+"F3.boolean.opBoolean","MERGE",FACE,{"derivedFrom":[subQ15,subQ19,subQ12,subQ16]});var subQ22=makeQuery(id+"F5.boolean.opBoolean","SPLIT",FACE,{"disambiguationData":[TD([makeQuery(id+"F5.opExtrude","SWEPT_FACE",FACE,{"disambiguationData":[OSD([sQuery(id+"F4.wireOp",EDGE,"E6.bottom")])]})])],"derivedFrom":subQ21});var subQ23=makeQuery(id+"F12.opPattern","COPY",FACE,{"derivedFrom":subQ22,"instanceName":"1"});var subQ24=makeQuery(id+"F5.boolean.opBoolean","SPLIT",FACE,{"disambiguationData":[TD([makeQuery(id+"F3.opExtrude","SWEPT_FACE",FACE,{"disambiguationData":[OSD([subQ3])]})])],"derivedFrom":subQ21});var subQ25=makeQuery(id+"F12.boolean.opBoolean","MERGE",FACE,{"derivedFrom":[subQ24,makeQuery(id+"F12.opPattern","COPY",FACE,{"derivedFrom":subQ24,"instanceName":"1"})]});Q0=makeQuery(id+"F23.boolean.opBoolean","MERGE",FACE,{"derivedFrom":[makeQuery(id+"F21.boolean.opBoolean","MERGE",FACE,{"derivedFrom":[subQ22,makeQuery(id+"F15.opPattern","COPY",FACE,{"derivedFrom":subQ22,"instanceName":"1"}),makeQuery(id+"F17.boolean.opBoolean","MERGE",FACE,{"derivedFrom":[subQ25,makeQuery(id+"F15.opPattern","COPY",FACE,{"derivedFrom":subQ25,"instanceName":"1"}),makeQuery(id+"F15.boolean.opBoolean","MERGE",FACE,{"derivedFrom":[subQ23,makeQuery(id+"F15.opPattern","COPY",FACE,{"derivedFrom":subQ23,"instanceName":"1"})]})],"fromTools":[makeQuery(id+"F17.opExtrude","CAP_FACE",FACE,{"disambiguationData":[OSD([sQuery(id+"F16.wireOp",EDGE,"E16.bottom"),sQuery(id+"F16.wireOp",EDGE,"E16.top"),sQuery(id+"F16.wireOp",EDGE,"E16.left"),sQuery(id+"F16.wireOp",EDGE,"E16.right")])],"isStart":false})]})],"fromTools":[makeQuery(id+"F21.opExtrude","SWEPT_FACE",FACE,{"disambiguationData":[OSD([subQ0]),TDD([makeQuery(id+"F20.imprint","IMPRINT",EDGE,{"disambiguationData":[TD([[makeQuery(id+"F20.imprint","INTERSECT",VERTEX,{"derivedFrom":[makeQuery(id+"F15.opPattern","COPY",EDGE,{"derivedFrom":subQ6,"instanceName":"1"}),subQ0]}),1.0],[makeQuery(id+"F20.imprint","INTERSECT",VERTEX,{"derivedFrom":[makeQuery(id+"F15.opPattern","COPY",EDGE,{"derivedFrom":subQ9,"instanceName":"1"}),sQuery(id+"F20.wireOp",EDGE,"E25"),subQ0]}),-1.0]])],"derivedFrom":subQ0})])]}),makeQuery(id+"F21.opExtrude","SWEPT_FACE",FACE,{"disambiguationData":[OSD([subQ0]),TDD([makeQuery(id+"F20.imprint","IMPRINT",EDGE,{"disambiguationData":[TD([[makeQuery(id+"F20.imprint","INTERSECT",VERTEX,{"derivedFrom":[subQ6,subQ0]}),-1.0],[makeQuery(id+"F20.imprint","INTERSECT",VERTEX,{"derivedFrom":[subQ9,sQuery(id+"F20.wireOp",EDGE,"E19"),subQ0]}),1.0]])],"derivedFrom":subQ0})])]})]}),makeQuery(id+"F23.opExtrude","CAP_FACE",FACE,{"disambiguationData":[OSD([sQuery(id+"F22.wireOp",EDGE,"E27"),sQuery(id+"F22.wireOp",EDGE,"E28"),sQuery(id+"F22.wireOp",EDGE,"E29"),sQuery(id+"F22.wireOp",EDGE,"E30"),sQuery(id+"F22.wireOp",EDGE,"E31"),sQuery(id+"F22.wireOp",EDGE,"E32"),sQuery(id+"F22.wireOp",EDGE,"E33"),sQuery(id+"F22.wireOp",EDGE,"E34")])],"isStart":false}),makeQuery(id+"F23.opExtrude","CAP_FACE",FACE,{"disambiguationData":[OSD([sQuery(id+"F22.wireOp",EDGE,"E35"),sQuery(id+"F22.wireOp",EDGE,"E36"),sQuery(id+"F22.wireOp",EDGE,"E37"),sQuery(id+"F22.wireOp",EDGE,"E38"),sQuery(id+"F22.wireOp",EDGE,"E39"),sQuery(id+"F22.wireOp",EDGE,"E40"),sQuery(id+"F22.wireOp",EDGE,"E41"),sQuery(id+"F22.wireOp",EDGE,"E42")])],"isStart":false})]});}
            var sketch = newSketch(context, id + "F27", { "sketchPlane" : qUnion([Q0])});
            skLineSegment(sketch, "E48.bottom", {"start": v(30, -720) * mm, "end": v(0, -720) * mm});
            skLineSegment(sketch, "E48.top", {"start": v(30, -750) * mm, "end": v(0, -750) * mm});
            skLineSegment(sketch, "E48.left", {"start": v(30, -720) * mm, "end": v(30, -750) * mm});
            skLineSegment(sketch, "E48.right", {"start": v(0, -720) * mm, "end": v(0, -750) * mm});
            skSolve(sketch);
        }
        {
            var Q0;
            {var subQ0=sQuery(id+"F20.wireOp",EDGE,"E26");var subQ1=sQuery(id+"F4.wireOp",EDGE,"E4.right");var subQ2=sQuery(id+"F4.wireOp",EDGE,"E4.bottom");var subQ3=sQuery(id+"F2.wireOp",EDGE,"E1.left");var subQ4=sQuery(id+"F2.wireOp",EDGE,"E1.top");var subQ5=sQuery(id+"F0.wireOp",EDGE,"E0.top");var subQ6=makeQuery(id+"F5.opExtrude","SWEPT_EDGE",EDGE,{"disambiguationData":[OSD([subQ5,subQ4,subQ3,subQ2,subQ1])]});var subQ7=sQuery(id+"F4.wireOp",EDGE,"E4.left");var subQ8=sQuery(id+"F0.wireOp",EDGE,"E0.left");var subQ9=makeQuery(id+"F5.boolean.opBoolean","MERGE",EDGE,{"derivedFrom":[makeQuery(id+"F1.opExtrude","CAP_EDGE",EDGE,{"disambiguationData":[OSD([subQ8])],"isStart":false}),makeQuery(id+"F5.opExtrude","SWEPT_EDGE",EDGE,{"disambiguationData":[OSD([subQ2,subQ7])]})]});var subQ12=makeQuery(id+"F3.opExtrude","SWEPT_FACE",FACE,{"disambiguationData":[OSD([sQuery(id+"F2.wireOp",EDGE,"E2.top")])]});var subQ15=makeQuery(id+"F1.opExtrude","SWEPT_FACE",FACE,{"disambiguationData":[OSD([subQ5])]});var subQ16=makeQuery(id+"F3.opExtrude","SWEPT_FACE",FACE,{"disambiguationData":[OSD([sQuery(id+"F2.wireOp",EDGE,"E3.top")])]});var subQ19=makeQuery(id+"F3.opExtrude","SWEPT_FACE",FACE,{"disambiguationData":[OSD([subQ4])]});var subQ21=makeQuery(id+"F3.boolean.opBoolean","MERGE",FACE,{"derivedFrom":[subQ15,subQ19,subQ12,subQ16]});var subQ22=makeQuery(id+"F5.boolean.opBoolean","SPLIT",FACE,{"disambiguationData":[TD([makeQuery(id+"F5.opExtrude","SWEPT_FACE",FACE,{"disambiguationData":[OSD([sQuery(id+"F4.wireOp",EDGE,"E6.bottom")])]})])],"derivedFrom":subQ21});var subQ23=makeQuery(id+"F12.opPattern","COPY",FACE,{"derivedFrom":subQ22,"instanceName":"1"});var subQ24=makeQuery(id+"F5.boolean.opBoolean","SPLIT",FACE,{"disambiguationData":[TD([makeQuery(id+"F3.opExtrude","SWEPT_FACE",FACE,{"disambiguationData":[OSD([subQ3])]})])],"derivedFrom":subQ21});var subQ25=makeQuery(id+"F12.boolean.opBoolean","MERGE",FACE,{"derivedFrom":[subQ24,makeQuery(id+"F12.opPattern","COPY",FACE,{"derivedFrom":subQ24,"instanceName":"1"})]});Q0=makeQuery(id+"F23.boolean.opBoolean","MERGE",FACE,{"derivedFrom":[makeQuery(id+"F21.boolean.opBoolean","MERGE",FACE,{"derivedFrom":[subQ22,makeQuery(id+"F15.opPattern","COPY",FACE,{"derivedFrom":subQ22,"instanceName":"1"}),makeQuery(id+"F17.boolean.opBoolean","MERGE",FACE,{"derivedFrom":[subQ25,makeQuery(id+"F15.opPattern","COPY",FACE,{"derivedFrom":subQ25,"instanceName":"1"}),makeQuery(id+"F15.boolean.opBoolean","MERGE",FACE,{"derivedFrom":[subQ23,makeQuery(id+"F15.opPattern","COPY",FACE,{"derivedFrom":subQ23,"instanceName":"1"})]})],"fromTools":[makeQuery(id+"F17.opExtrude","CAP_FACE",FACE,{"disambiguationData":[OSD([sQuery(id+"F16.wireOp",EDGE,"E16.bottom"),sQuery(id+"F16.wireOp",EDGE,"E16.top"),sQuery(id+"F16.wireOp",EDGE,"E16.left"),sQuery(id+"F16.wireOp",EDGE,"E16.right")])],"isStart":false})]})],"fromTools":[makeQuery(id+"F21.opExtrude","SWEPT_FACE",FACE,{"disambiguationData":[OSD([subQ0]),TDD([makeQuery(id+"F20.imprint","IMPRINT",EDGE,{"disambiguationData":[TD([[makeQuery(id+"F20.imprint","INTERSECT",VERTEX,{"derivedFrom":[makeQuery(id+"F15.opPattern","COPY",EDGE,{"derivedFrom":subQ6,"instanceName":"1"}),subQ0]}),1.0],[makeQuery(id+"F20.imprint","INTERSECT",VERTEX,{"derivedFrom":[makeQuery(id+"F15.opPattern","COPY",EDGE,{"derivedFrom":subQ9,"instanceName":"1"}),sQuery(id+"F20.wireOp",EDGE,"E25"),subQ0]}),-1.0]])],"derivedFrom":subQ0})])]}),makeQuery(id+"F21.opExtrude","SWEPT_FACE",FACE,{"disambiguationData":[OSD([subQ0]),TDD([makeQuery(id+"F20.imprint","IMPRINT",EDGE,{"disambiguationData":[TD([[makeQuery(id+"F20.imprint","INTERSECT",VERTEX,{"derivedFrom":[subQ6,subQ0]}),-1.0],[makeQuery(id+"F20.imprint","INTERSECT",VERTEX,{"derivedFrom":[subQ9,sQuery(id+"F20.wireOp",EDGE,"E19"),subQ0]}),1.0]])],"derivedFrom":subQ0})])]})]}),makeQuery(id+"F23.opExtrude","CAP_FACE",FACE,{"disambiguationData":[OSD([sQuery(id+"F22.wireOp",EDGE,"E27"),sQuery(id+"F22.wireOp",EDGE,"E28"),sQuery(id+"F22.wireOp",EDGE,"E29"),sQuery(id+"F22.wireOp",EDGE,"E30"),sQuery(id+"F22.wireOp",EDGE,"E31"),sQuery(id+"F22.wireOp",EDGE,"E32"),sQuery(id+"F22.wireOp",EDGE,"E33"),sQuery(id+"F22.wireOp",EDGE,"E34")])],"isStart":false}),makeQuery(id+"F23.opExtrude","CAP_FACE",FACE,{"disambiguationData":[OSD([sQuery(id+"F22.wireOp",EDGE,"E35"),sQuery(id+"F22.wireOp",EDGE,"E36"),sQuery(id+"F22.wireOp",EDGE,"E37"),sQuery(id+"F22.wireOp",EDGE,"E38"),sQuery(id+"F22.wireOp",EDGE,"E39"),sQuery(id+"F22.wireOp",EDGE,"E40"),sQuery(id+"F22.wireOp",EDGE,"E41"),sQuery(id+"F22.wireOp",EDGE,"E42")])],"isStart":false})]});}
            var sketch = newSketch(context, id + "F28", { "sketchPlane" : qUnion([Q0])});
            skLineSegment(sketch, "E49", {"start": v(140.04, -997.06) * mm, "end": v(170.75, -997.06) * mm});
            skLineSegment(sketch, "E50", {"start": v(170.75, -997.06) * mm, "end": v(181.73, -947.06) * mm});
            skLineSegment(sketch, "E51", {"start": v(181.73, -947.06) * mm, "end": v(151.02, -947.06) * mm});
            skLineSegment(sketch, "E52", {"start": v(151.02, -947.06) * mm, "end": v(140.04, -997.06) * mm});
            skSolve(sketch);
        }
        {
            var Q1;
            Q1=makeQuery(id+"F28.imprint","IMPRINT",FACE,{"disambiguationData":[TD([[makeQuery(id+"F28.imprint","IMPRINT",EDGE,{"derivedFrom":sQuery(id+"F28.wireOp",EDGE,"E49")}),1.0]])]});
            var Q2;
            {var subQ1=makeQuery(id+"F11.opExtrude","SWEPT_FACE",FACE,{"disambiguationData":[OSD([sQuery(id+"F10.wireOp",EDGE,"E12.top")])]});var subQ5=sQuery(id+"F4.wireOp",EDGE,"E4.bottom");var subQ16=makeQuery(id+"F11.boolean.opBoolean","MERGE",FACE,{"derivedFrom":[makeQuery(id+"F5.boolean.opBoolean","MERGE",FACE,{"derivedFrom":[makeQuery(id+"F3.boolean.opBoolean","MERGE",FACE,{"derivedFrom":[makeQuery(id+"F1.opExtrude","CAP_FACE",FACE,{"disambiguationData":[OSD([sQuery(id+"F0.wireOp",EDGE,"E0.bottom"),sQuery(id+"F0.wireOp",EDGE,"E0.top"),sQuery(id+"F0.wireOp",EDGE,"E0.left"),sQuery(id+"F0.wireOp",EDGE,"E0.right")])],"isStart":false}),makeQuery(id+"F3.opExtrude","SWEPT_FACE",FACE,{"disambiguationData":[OSD([sQuery(id+"F2.wireOp",EDGE,"E1.left")])]})]}),makeQuery(id+"F5.opExtrude","SWEPT_FACE",FACE,{"disambiguationData":[OSD([subQ5])]})]}),makeQuery(id+"F11.opExtrude","SWEPT_FACE",FACE,{"disambiguationData":[OSD([sQuery(id+"F10.wireOp",EDGE,"E12.left")])]})]});var subQ17=makeQuery(id+"F12.boolean.opBoolean","MERGE",FACE,{"derivedFrom":[subQ16,makeQuery(id+"F12.opPattern","COPY",FACE,{"derivedFrom":subQ16,"instanceName":"1"})]});Q2=makeQuery(id+"F21.boolean.opBoolean","SPLIT",FACE,{"disambiguationData":[TD([subQ1])],"derivedFrom":makeQuery(id+"F15.boolean.opBoolean","MERGE",FACE,{"derivedFrom":[subQ17,makeQuery(id+"F15.opPattern","COPY",FACE,{"derivedFrom":subQ17,"instanceName":"1"})]})});}
            loft(context, id + "F29", {"operationType" : NewBodyOperationType.ADD, "sheetProfilesArray" : [{ "sheetProfileEntities" : qUnion([Q1]) }, { "sheetProfileEntities" : qUnion([Q2]) }]});
        }
        {
            var Q0;
            {var subQ0=sQuery(id+"F20.wireOp",EDGE,"E26");var subQ1=sQuery(id+"F4.wireOp",EDGE,"E4.right");var subQ2=sQuery(id+"F4.wireOp",EDGE,"E4.bottom");var subQ3=sQuery(id+"F2.wireOp",EDGE,"E1.left");var subQ4=sQuery(id+"F2.wireOp",EDGE,"E1.top");var subQ5=sQuery(id+"F0.wireOp",EDGE,"E0.top");var subQ6=makeQuery(id+"F5.opExtrude","SWEPT_EDGE",EDGE,{"disambiguationData":[OSD([subQ5,subQ4,subQ3,subQ2,subQ1])]});var subQ7=sQuery(id+"F4.wireOp",EDGE,"E4.left");var subQ8=sQuery(id+"F0.wireOp",EDGE,"E0.left");var subQ9=makeQuery(id+"F5.boolean.opBoolean","MERGE",EDGE,{"derivedFrom":[makeQuery(id+"F1.opExtrude","CAP_EDGE",EDGE,{"disambiguationData":[OSD([subQ8])],"isStart":false}),makeQuery(id+"F5.opExtrude","SWEPT_EDGE",EDGE,{"disambiguationData":[OSD([subQ2,subQ7])]})]});var subQ12=makeQuery(id+"F3.opExtrude","SWEPT_FACE",FACE,{"disambiguationData":[OSD([sQuery(id+"F2.wireOp",EDGE,"E2.top")])]});var subQ15=makeQuery(id+"F1.opExtrude","SWEPT_FACE",FACE,{"disambiguationData":[OSD([subQ5])]});var subQ16=makeQuery(id+"F3.opExtrude","SWEPT_FACE",FACE,{"disambiguationData":[OSD([sQuery(id+"F2.wireOp",EDGE,"E3.top")])]});var subQ19=makeQuery(id+"F3.opExtrude","SWEPT_FACE",FACE,{"disambiguationData":[OSD([subQ4])]});var subQ21=makeQuery(id+"F3.boolean.opBoolean","MERGE",FACE,{"derivedFrom":[subQ15,subQ19,subQ12,subQ16]});var subQ22=makeQuery(id+"F5.boolean.opBoolean","SPLIT",FACE,{"disambiguationData":[TD([makeQuery(id+"F5.opExtrude","SWEPT_FACE",FACE,{"disambiguationData":[OSD([sQuery(id+"F4.wireOp",EDGE,"E6.bottom")])]})])],"derivedFrom":subQ21});var subQ23=makeQuery(id+"F12.opPattern","COPY",FACE,{"derivedFrom":subQ22,"instanceName":"1"});var subQ24=makeQuery(id+"F5.boolean.opBoolean","SPLIT",FACE,{"disambiguationData":[TD([makeQuery(id+"F3.opExtrude","SWEPT_FACE",FACE,{"disambiguationData":[OSD([subQ3])]})])],"derivedFrom":subQ21});var subQ25=makeQuery(id+"F12.boolean.opBoolean","MERGE",FACE,{"derivedFrom":[subQ24,makeQuery(id+"F12.opPattern","COPY",FACE,{"derivedFrom":subQ24,"instanceName":"1"})]});Q0=makeQuery(id+"F23.boolean.opBoolean","MERGE",FACE,{"derivedFrom":[makeQuery(id+"F21.boolean.opBoolean","MERGE",FACE,{"derivedFrom":[subQ22,makeQuery(id+"F15.opPattern","COPY",FACE,{"derivedFrom":subQ22,"instanceName":"1"}),makeQuery(id+"F17.boolean.opBoolean","MERGE",FACE,{"derivedFrom":[subQ25,makeQuery(id+"F15.opPattern","COPY",FACE,{"derivedFrom":subQ25,"instanceName":"1"}),makeQuery(id+"F15.boolean.opBoolean","MERGE",FACE,{"derivedFrom":[subQ23,makeQuery(id+"F15.opPattern","COPY",FACE,{"derivedFrom":subQ23,"instanceName":"1"})]})],"fromTools":[makeQuery(id+"F17.opExtrude","CAP_FACE",FACE,{"disambiguationData":[OSD([sQuery(id+"F16.wireOp",EDGE,"E16.bottom"),sQuery(id+"F16.wireOp",EDGE,"E16.top"),sQuery(id+"F16.wireOp",EDGE,"E16.left"),sQuery(id+"F16.wireOp",EDGE,"E16.right")])],"isStart":false})]})],"fromTools":[makeQuery(id+"F21.opExtrude","SWEPT_FACE",FACE,{"disambiguationData":[OSD([subQ0]),TDD([makeQuery(id+"F20.imprint","IMPRINT",EDGE,{"disambiguationData":[TD([[makeQuery(id+"F20.imprint","INTERSECT",VERTEX,{"derivedFrom":[makeQuery(id+"F15.opPattern","COPY",EDGE,{"derivedFrom":subQ6,"instanceName":"1"}),subQ0]}),1.0],[makeQuery(id+"F20.imprint","INTERSECT",VERTEX,{"derivedFrom":[makeQuery(id+"F15.opPattern","COPY",EDGE,{"derivedFrom":subQ9,"instanceName":"1"}),sQuery(id+"F20.wireOp",EDGE,"E25"),subQ0]}),-1.0]])],"derivedFrom":subQ0})])]}),makeQuery(id+"F21.opExtrude","SWEPT_FACE",FACE,{"disambiguationData":[OSD([subQ0]),TDD([makeQuery(id+"F20.imprint","IMPRINT",EDGE,{"disambiguationData":[TD([[makeQuery(id+"F20.imprint","INTERSECT",VERTEX,{"derivedFrom":[subQ6,subQ0]}),-1.0],[makeQuery(id+"F20.imprint","INTERSECT",VERTEX,{"derivedFrom":[subQ9,sQuery(id+"F20.wireOp",EDGE,"E19"),subQ0]}),1.0]])],"derivedFrom":subQ0})])]})]}),makeQuery(id+"F23.opExtrude","CAP_FACE",FACE,{"disambiguationData":[OSD([sQuery(id+"F22.wireOp",EDGE,"E27"),sQuery(id+"F22.wireOp",EDGE,"E28"),sQuery(id+"F22.wireOp",EDGE,"E29"),sQuery(id+"F22.wireOp",EDGE,"E30"),sQuery(id+"F22.wireOp",EDGE,"E31"),sQuery(id+"F22.wireOp",EDGE,"E32"),sQuery(id+"F22.wireOp",EDGE,"E33"),sQuery(id+"F22.wireOp",EDGE,"E34")])],"isStart":false}),makeQuery(id+"F23.opExtrude","CAP_FACE",FACE,{"disambiguationData":[OSD([sQuery(id+"F22.wireOp",EDGE,"E35"),sQuery(id+"F22.wireOp",EDGE,"E36"),sQuery(id+"F22.wireOp",EDGE,"E37"),sQuery(id+"F22.wireOp",EDGE,"E38"),sQuery(id+"F22.wireOp",EDGE,"E39"),sQuery(id+"F22.wireOp",EDGE,"E40"),sQuery(id+"F22.wireOp",EDGE,"E41"),sQuery(id+"F22.wireOp",EDGE,"E42")])],"isStart":false})]});}
            var sketch = newSketch(context, id + "F30", { "sketchPlane" : qUnion([Q0])});
            skLineSegment(sketch, "E53", {"start": v(399.25, -997.06) * mm, "end": v(429.96, -997.06) * mm});
            skLineSegment(sketch, "E54", {"start": v(429.96, -997.06) * mm, "end": v(418.98, -947.06) * mm});
            skLineSegment(sketch, "E55", {"start": v(399.25, -997.06) * mm, "end": v(388.27, -947.06) * mm});
            skLineSegment(sketch, "E56", {"start": v(388.27, -947.06) * mm, "end": v(418.98, -947.06) * mm});
            skSolve(sketch);
        }
        {
            var Q1;
            Q1=makeQuery(id+"F30.imprint","IMPRINT",FACE,{"disambiguationData":[TD([[makeQuery(id+"F30.imprint","IMPRINT",EDGE,{"derivedFrom":sQuery(id+"F30.wireOp",EDGE,"E53")}),1.0]])]});
            var Q2;
            {var subQ7=sQuery(id+"F4.wireOp",EDGE,"E4.bottom");var subQ16=makeQuery(id+"F11.boolean.opBoolean","MERGE",FACE,{"derivedFrom":[makeQuery(id+"F5.boolean.opBoolean","MERGE",FACE,{"derivedFrom":[makeQuery(id+"F3.boolean.opBoolean","MERGE",FACE,{"derivedFrom":[makeQuery(id+"F1.opExtrude","CAP_FACE",FACE,{"disambiguationData":[OSD([sQuery(id+"F0.wireOp",EDGE,"E0.bottom"),sQuery(id+"F0.wireOp",EDGE,"E0.top"),sQuery(id+"F0.wireOp",EDGE,"E0.left"),sQuery(id+"F0.wireOp",EDGE,"E0.right")])],"isStart":false}),makeQuery(id+"F3.opExtrude","SWEPT_FACE",FACE,{"disambiguationData":[OSD([sQuery(id+"F2.wireOp",EDGE,"E1.left")])]})]}),makeQuery(id+"F5.opExtrude","SWEPT_FACE",FACE,{"disambiguationData":[OSD([subQ7])]})]}),makeQuery(id+"F11.opExtrude","SWEPT_FACE",FACE,{"disambiguationData":[OSD([sQuery(id+"F10.wireOp",EDGE,"E12.left")])]})]});var subQ17=makeQuery(id+"F12.boolean.opBoolean","MERGE",FACE,{"derivedFrom":[subQ16,makeQuery(id+"F12.opPattern","COPY",FACE,{"derivedFrom":subQ16,"instanceName":"1"})]});Q2=makeQuery(id+"F21.boolean.opBoolean","SPLIT",FACE,{"disambiguationData":[TD([makeQuery(id+"F17.boolean.opBoolean","COPY",FACE,{"derivedFrom":makeQuery(id+"F17.opExtrude","SWEPT_FACE",FACE,{"disambiguationData":[OSD([sQuery(id+"F16.wireOp",EDGE,"E16.right")])]})})])],"derivedFrom":makeQuery(id+"F15.boolean.opBoolean","MERGE",FACE,{"derivedFrom":[subQ17,makeQuery(id+"F15.opPattern","COPY",FACE,{"derivedFrom":subQ17,"instanceName":"1"})]})});}
            loft(context, id + "F31", {"operationType" : NewBodyOperationType.ADD, "sheetProfilesArray" : [{ "sheetProfileEntities" : qUnion([Q1]) }, { "sheetProfileEntities" : qUnion([Q2]) }]});
        }
        {
            var Q0;
            {var subQ0=makeQuery(id+"F11.opExtrude","SWEPT_FACE",FACE,{"disambiguationData":[OSD([sQuery(id+"F10.wireOp",EDGE,"E12.top")])]});var subQ1=makeQuery(id+"F11.opExtrude","SWEPT_FACE",FACE,{"disambiguationData":[OSD([sQuery(id+"F10.wireOp",EDGE,"E13.bottom")])]});Q0=makeQuery(id+"F19.boolean.opBoolean","MERGE",FACE,{"derivedFrom":[makeQuery(id+"F15.opPattern","COPY",FACE,{"derivedFrom":makeQuery(id+"F12.boolean.opBoolean","MERGE",FACE,{"derivedFrom":[subQ1,makeQuery(id+"F12.opPattern","COPY",FACE,{"derivedFrom":subQ1,"instanceName":"1"})]}),"instanceName":"1"}),makeQuery(id+"F15.opPattern","COPY",FACE,{"derivedFrom":makeQuery(id+"F12.boolean.opBoolean","MERGE",FACE,{"derivedFrom":[subQ0,makeQuery(id+"F12.opPattern","COPY",FACE,{"derivedFrom":subQ0,"instanceName":"1"})]}),"instanceName":"1"}),makeQuery(id+"F19.opExtrude","CAP_FACE",FACE,{"disambiguationData":[OSD([sQuery(id+"F18.wireOp",EDGE,"E18.bottom"),sQuery(id+"F18.wireOp",EDGE,"E18.top"),sQuery(id+"F18.wireOp",EDGE,"E18.left"),sQuery(id+"F18.wireOp",EDGE,"E18.right")])],"isStart":false})]});}
            var sketch = newSketch(context, id + "F32", { "sketchPlane" : qUnion([Q0])});
            skLineSegment(sketch, "E57.bottom", {"start": v(345, 750) * mm, "end": v(375, 750) * mm});
            skLineSegment(sketch, "E57.top", {"start": v(345, 720) * mm, "end": v(375, 720) * mm});
            skLineSegment(sketch, "E57.left", {"start": v(345, 750) * mm, "end": v(345, 720) * mm});
            skLineSegment(sketch, "E57.right", {"start": v(375, 750) * mm, "end": v(375, 720) * mm});
            skPoint(sketch, "E58.firstSnap0", {"position": v(360, 720) * mm});
            skLineSegment(sketch, "E58.bottom", {"start": v(225, 720) * mm, "end": v(195, 720) * mm});
            skLineSegment(sketch, "E58.top", {"start": v(225, 750) * mm, "end": v(195, 750) * mm});
            skLineSegment(sketch, "E58.left", {"start": v(225, 720) * mm, "end": v(225, 750) * mm});
            skLineSegment(sketch, "E58.right", {"start": v(195, 720) * mm, "end": v(195, 750) * mm});
            skSolve(sketch);
        }
        {
            var Q0;
            Q0 = qSketchRegion(id + "F32", true);
            extrude(context, id + "F33", {"entities" : qUnion([Q0]), "operationType" : NewBodyOperationType.ADD, "endBound" : BoundingType.UP_TO_NEXT, "depth" : 25 * mm, "offsetDistance" : 25 * mm});
        }
        {
            var Q0;
            Q0=makeQuery(id+"F33.boolean.opBoolean","MERGE",FACE,{"derivedFrom":[makeQuery(id+"F21.boolean.opBoolean","MERGE",FACE,{"derivedFrom":[makeQuery(id+"F19.opExtrude","SWEPT_FACE",FACE,{"disambiguationData":[OSD([sQuery(id+"F18.wireOp",EDGE,"E17.right")])]})],"fromTools":[makeQuery(id+"F21.opExtrude","SWEPT_FACE",FACE,{"disambiguationData":[OSD([sQuery(id+"F20.wireOp",EDGE,"E21")])]})]}),makeQuery(id+"F33.opExtrude","SWEPT_FACE",FACE,{"disambiguationData":[OSD([sQuery(id+"F32.wireOp",EDGE,"E58.right")])]})]});
            var sketch = newSketch(context, id + "F34", { "sketchPlane" : qUnion([Q0])});
            skLineSegment(sketch, "E59.bottom", {"start": v(750, 170) * mm, "end": v(720, 170) * mm});
            skLineSegment(sketch, "E59.top", {"start": v(750, 140) * mm, "end": v(720, 140) * mm});
            skLineSegment(sketch, "E59.left", {"start": v(750, 170) * mm, "end": v(750, 140) * mm});
            skLineSegment(sketch, "E59.right", {"start": v(720, 170) * mm, "end": v(720, 140) * mm});
            skSolve(sketch);
        }
        {
            var Q1;
            Q1=makeQuery(id+"F34.imprint","IMPRINT",FACE,{"disambiguationData":[TD([[makeQuery(id+"F34.imprint","IMPRINT",EDGE,{"derivedFrom":sQuery(id+"F34.wireOp",EDGE,"E59.bottom")}),1.0]])]});
            var Q2;
            Q2=makeQuery(id+"F27.imprint","IMPRINT",FACE,{"disambiguationData":[TD([[makeQuery(id+"F27.imprint","IMPRINT",EDGE,{"derivedFrom":sQuery(id+"F27.wireOp",EDGE,"E48.bottom")}),1.0]])]});
            loft(context, id + "F35", {"operationType" : NewBodyOperationType.ADD, "sheetProfilesArray" : [{ "sheetProfileEntities" : qUnion([Q1]) }, { "sheetProfileEntities" : qUnion([Q2]) }]});
        }
        {
            var Q0;
            Q0=makeQuery(id+"F33.boolean.opBoolean","MERGE",FACE,{"derivedFrom":[makeQuery(id+"F21.boolean.opBoolean","MERGE",FACE,{"derivedFrom":[makeQuery(id+"F19.opExtrude","SWEPT_FACE",FACE,{"disambiguationData":[OSD([sQuery(id+"F18.wireOp",EDGE,"E18.right")])]})],"fromTools":[makeQuery(id+"F21.opExtrude","SWEPT_FACE",FACE,{"disambiguationData":[OSD([sQuery(id+"F20.wireOp",EDGE,"E23")])]})]}),makeQuery(id+"F33.opExtrude","SWEPT_FACE",FACE,{"disambiguationData":[OSD([sQuery(id+"F32.wireOp",EDGE,"E57.right")])]})]});
            var sketch = newSketch(context, id + "F36", { "sketchPlane" : qUnion([Q0])});
            skLineSegment(sketch, "E60.bottom", {"start": v(-750, 170) * mm, "end": v(-720, 170) * mm});
            skLineSegment(sketch, "E60.top", {"start": v(-750, 140) * mm, "end": v(-720, 140) * mm});
            skLineSegment(sketch, "E60.left", {"start": v(-750, 170) * mm, "end": v(-750, 140) * mm});
            skLineSegment(sketch, "E60.right", {"start": v(-720, 170) * mm, "end": v(-720, 140) * mm});
            skSolve(sketch);
        }
        {
            var Q1;
            Q1=makeQuery(id+"F36.imprint","IMPRINT",FACE,{"disambiguationData":[TD([[makeQuery(id+"F36.imprint","IMPRINT",EDGE,{"derivedFrom":sQuery(id+"F36.wireOp",EDGE,"E60.bottom")}),-1.0]])]});
            var Q2;
            Q2=makeQuery(id+"F26.imprint","IMPRINT",FACE,{"disambiguationData":[TD([[makeQuery(id+"F26.imprint","IMPRINT",EDGE,{"derivedFrom":sQuery(id+"F26.wireOp",EDGE,"E47.bottom")}),-1.0]])]});
            loft(context, id + "F37", {"operationType" : NewBodyOperationType.ADD, "sheetProfilesArray" : [{ "sheetProfileEntities" : qUnion([Q1]) }, { "sheetProfileEntities" : qUnion([Q2]) }]});
        }
        {
            var Q1;
            {var subQ0=sQuery(id+"F18.wireOp",EDGE,"E17.right");var subQ8=sQuery(id+"F32.wireOp",EDGE,"E58.right");var subQ14=sQuery(id+"F20.wireOp",EDGE,"E21");var subQ33=sQuery(id+"F4.wireOp",EDGE,"E6.bottom");var subQ42=makeQuery(id+"F5.opExtrude","SWEPT_FACE",FACE,{"disambiguationData":[OSD([subQ33])]});var subQ45=makeQuery(id+"F33.opExtrude","SWEPT_FACE",FACE,{"disambiguationData":[OSD([subQ8])]});var subQ49=makeQuery(id+"F19.opExtrude","SWEPT_FACE",FACE,{"disambiguationData":[OSD([subQ0])]});Q1=makeQuery(id+"F35.boolean.opBoolean","SPLIT",FACE,{"disambiguationData":[TD([subQ42])],"derivedFrom":makeQuery(id+"F33.boolean.opBoolean","MERGE",FACE,{"derivedFrom":[makeQuery(id+"F21.boolean.opBoolean","MERGE",FACE,{"derivedFrom":[subQ49],"fromTools":[makeQuery(id+"F21.opExtrude","SWEPT_FACE",FACE,{"disambiguationData":[OSD([subQ14])]})]}),subQ45]})});}
            var Q2;
            {var subQ0=sQuery(id+"F4.wireOp",EDGE,"E4.right");var subQ3=sQuery(id+"F4.wireOp",EDGE,"E4.left");var subQ5=makeQuery(id+"F3.opExtrude","SWEPT_FACE",FACE,{"disambiguationData":[OSD([sQuery(id+"F2.wireOp",EDGE,"E2.top")])]});var subQ8=sQuery(id+"F0.wireOp",EDGE,"E0.top");var subQ9=makeQuery(id+"F1.opExtrude","SWEPT_FACE",FACE,{"disambiguationData":[OSD([subQ8])]});var subQ10=makeQuery(id+"F3.opExtrude","SWEPT_FACE",FACE,{"disambiguationData":[OSD([sQuery(id+"F2.wireOp",EDGE,"E3.top")])]});var subQ14=sQuery(id+"F0.wireOp",EDGE,"E0.left");var subQ15=makeQuery(id+"F1.opExtrude","SWEPT_FACE",FACE,{"disambiguationData":[OSD([subQ14])]});var subQ16=sQuery(id+"F2.wireOp",EDGE,"E1.top");var subQ17=makeQuery(id+"F3.opExtrude","SWEPT_FACE",FACE,{"disambiguationData":[OSD([subQ16])]});var subQ18=makeQuery(id+"F5.opExtrude","SWEPT_FACE",FACE,{"disambiguationData":[OSD([sQuery(id+"F4.wireOp",EDGE,"E6.bottom")])]});var subQ21=makeQuery(id+"F3.boolean.opBoolean","MERGE",FACE,{"derivedFrom":[subQ9,subQ17,subQ5,subQ10]});var subQ22=makeQuery(id+"F5.boolean.opBoolean","SPLIT",FACE,{"disambiguationData":[TD([subQ18])],"derivedFrom":subQ21});var subQ23=makeQuery(id+"F12.opPattern","COPY",FACE,{"derivedFrom":subQ22,"instanceName":"1"});var subQ24=sQuery(id+"F4.wireOp",EDGE,"E4.bottom");var subQ28=sQuery(id+"F2.wireOp",EDGE,"E1.left");var subQ29=makeQuery(id+"F3.opExtrude","SWEPT_FACE",FACE,{"disambiguationData":[OSD([subQ28])]});var subQ31=makeQuery(id+"F5.boolean.opBoolean","SPLIT",FACE,{"disambiguationData":[TD([subQ29])],"derivedFrom":subQ21});var subQ32=makeQuery(id+"F12.opPattern","COPY",FACE,{"derivedFrom":subQ31,"instanceName":"1"});var subQ33=makeQuery(id+"F15.opPattern","COPY",FACE,{"derivedFrom":subQ22,"instanceName":"1"});var subQ36=makeQuery(id+"F12.boolean.opBoolean","MERGE",FACE,{"derivedFrom":[subQ31,subQ32]});var subQ37=makeQuery(id+"F15.opPattern","COPY",FACE,{"derivedFrom":subQ36,"instanceName":"1"});var subQ43=subQ23;var subQ44=makeQuery(id+"F15.opPattern","COPY",FACE,{"derivedFrom":subQ43,"instanceName":"1"});var subQ59=sQuery(id+"F22.wireOp",EDGE,"E42");var subQ60=sQuery(id+"F22.wireOp",EDGE,"E41");var subQ61=sQuery(id+"F22.wireOp",EDGE,"E39");var subQ62=sQuery(id+"F22.wireOp",EDGE,"E38");var subQ63=sQuery(id+"F22.wireOp",EDGE,"E37");var subQ64=sQuery(id+"F22.wireOp",EDGE,"E36");var subQ65=sQuery(id+"F22.wireOp",EDGE,"E35");var subQ66=makeQuery(id+"F23.opExtrude","CAP_FACE",FACE,{"disambiguationData":[OSD([subQ65,subQ64,subQ63,subQ62,subQ61,subQ60,subQ59])],"isStart":false});var subQ67=sQuery(id+"F22.wireOp",EDGE,"E34");var subQ68=sQuery(id+"F22.wireOp",EDGE,"E33");var subQ69=sQuery(id+"F22.wireOp",EDGE,"E31");var subQ70=sQuery(id+"F22.wireOp",EDGE,"E30");var subQ71=sQuery(id+"F22.wireOp",EDGE,"E29");var subQ72=sQuery(id+"F22.wireOp",EDGE,"E28");var subQ73=sQuery(id+"F22.wireOp",EDGE,"E27");var subQ74=makeQuery(id+"F23.opExtrude","CAP_FACE",FACE,{"disambiguationData":[OSD([subQ73,subQ72,subQ71,subQ70,subQ69,subQ68,subQ67])],"isStart":false});var subQ86=sQuery(id+"F20.wireOp",EDGE,"E26");var subQ88=sQuery(id+"F20.wireOp",EDGE,"E19");var subQ97=sQuery(id+"F16.wireOp",EDGE,"E16.left");var subQ98=sQuery(id+"F16.wireOp",EDGE,"E16.top");var subQ109=makeQuery(id+"F5.opExtrude","SWEPT_EDGE",EDGE,{"disambiguationData":[OSD([subQ8,subQ16,subQ28,subQ24,subQ0])]});var subQ110=makeQuery(id+"F5.boolean.opBoolean","MERGE",EDGE,{"derivedFrom":[makeQuery(id+"F1.opExtrude","CAP_EDGE",EDGE,{"disambiguationData":[OSD([subQ14])],"isStart":false}),makeQuery(id+"F5.opExtrude","SWEPT_EDGE",EDGE,{"disambiguationData":[OSD([subQ24,subQ3])]})]});Q2=makeQuery(id+"F35.boolean.opBoolean","SPLIT",FACE,{"disambiguationData":[TD([subQ18])],"derivedFrom":makeQuery(id+"F33.boolean.opBoolean","SPLIT",FACE,{"disambiguationData":[TD([subQ15])],"derivedFrom":makeQuery(id+"F23.boolean.opBoolean","MERGE",FACE,{"derivedFrom":[makeQuery(id+"F21.boolean.opBoolean","MERGE",FACE,{"derivedFrom":[subQ22,subQ33,makeQuery(id+"F17.boolean.opBoolean","MERGE",FACE,{"derivedFrom":[subQ36,subQ37,makeQuery(id+"F15.boolean.opBoolean","MERGE",FACE,{"derivedFrom":[subQ43,subQ44]})],"fromTools":[makeQuery(id+"F17.opExtrude","CAP_FACE",FACE,{"disambiguationData":[OSD([sQuery(id+"F16.wireOp",EDGE,"E16.bottom"),subQ98,subQ97,sQuery(id+"F16.wireOp",EDGE,"E16.right")])],"isStart":false})]})],"fromTools":[makeQuery(id+"F21.opExtrude","SWEPT_FACE",FACE,{"disambiguationData":[OSD([subQ86]),TDD([makeQuery(id+"F20.imprint","IMPRINT",EDGE,{"disambiguationData":[TD([[makeQuery(id+"F20.imprint","INTERSECT",VERTEX,{"derivedFrom":[makeQuery(id+"F15.opPattern","COPY",EDGE,{"derivedFrom":subQ109,"instanceName":"1"}),subQ86]}),1.0],[makeQuery(id+"F20.imprint","INTERSECT",VERTEX,{"derivedFrom":[makeQuery(id+"F15.opPattern","COPY",EDGE,{"derivedFrom":subQ110,"instanceName":"1"}),sQuery(id+"F20.wireOp",EDGE,"E25"),subQ86]}),-1.0]])],"derivedFrom":subQ86})])]}),makeQuery(id+"F21.opExtrude","SWEPT_FACE",FACE,{"disambiguationData":[OSD([subQ86]),TDD([makeQuery(id+"F20.imprint","IMPRINT",EDGE,{"disambiguationData":[TD([[makeQuery(id+"F20.imprint","INTERSECT",VERTEX,{"derivedFrom":[subQ109,subQ86]}),-1.0],[makeQuery(id+"F20.imprint","INTERSECT",VERTEX,{"derivedFrom":[subQ110,subQ88,subQ86]}),1.0]])],"derivedFrom":subQ86})])]})]}),subQ74,subQ66]})})});}
            loft(context, id + "F38", {"operationType" : NewBodyOperationType.ADD, "sheetProfilesArray" : [{ "sheetProfileEntities" : qUnion([Q1]) }, { "sheetProfileEntities" : qUnion([Q2]) }]});
        }
        {
            var Q1;
            {var subQ0=sQuery(id+"F18.wireOp",EDGE,"E18.right");var subQ1=makeQuery(id+"F19.opExtrude","SWEPT_FACE",FACE,{"disambiguationData":[OSD([subQ0])]});var subQ2=makeQuery(id+"F7.opExtrude","SWEPT_FACE",FACE,{"disambiguationData":[OSD([sQuery(id+"F6.wireOp",EDGE,"E7.bottom")])]});var subQ11=sQuery(id+"F32.wireOp",EDGE,"E57.right");var subQ16=sQuery(id+"F20.wireOp",EDGE,"E23");var subQ49=makeQuery(id+"F33.opExtrude","SWEPT_FACE",FACE,{"disambiguationData":[OSD([subQ11])]});Q1=makeQuery(id+"F37.boolean.opBoolean","SPLIT",FACE,{"disambiguationData":[TD([subQ2])],"derivedFrom":makeQuery(id+"F33.boolean.opBoolean","MERGE",FACE,{"derivedFrom":[makeQuery(id+"F21.boolean.opBoolean","MERGE",FACE,{"derivedFrom":[subQ1],"fromTools":[makeQuery(id+"F21.opExtrude","SWEPT_FACE",FACE,{"disambiguationData":[OSD([subQ16])]})]}),subQ49]})});}
            var Q2;
            {var subQ0=sQuery(id+"F22.wireOp",EDGE,"E34");var subQ1=sQuery(id+"F22.wireOp",EDGE,"E33");var subQ2=sQuery(id+"F22.wireOp",EDGE,"E31");var subQ3=sQuery(id+"F22.wireOp",EDGE,"E30");var subQ4=sQuery(id+"F22.wireOp",EDGE,"E29");var subQ5=sQuery(id+"F22.wireOp",EDGE,"E28");var subQ6=sQuery(id+"F22.wireOp",EDGE,"E27");var subQ7=makeQuery(id+"F23.opExtrude","CAP_FACE",FACE,{"disambiguationData":[OSD([subQ6,subQ5,subQ4,subQ3,subQ2,subQ1,subQ0])],"isStart":false});var subQ8=makeQuery(id+"F3.opExtrude","SWEPT_FACE",FACE,{"disambiguationData":[OSD([sQuery(id+"F2.wireOp",EDGE,"E3.top")])]});var subQ9=makeQuery(id+"F5.opExtrude","SWEPT_FACE",FACE,{"disambiguationData":[OSD([sQuery(id+"F4.wireOp",EDGE,"E6.bottom")])]});var subQ10=subQ9;var subQ13=sQuery(id+"F4.wireOp",EDGE,"E4.right");var subQ16=sQuery(id+"F4.wireOp",EDGE,"E4.left");var subQ18=makeQuery(id+"F3.opExtrude","SWEPT_FACE",FACE,{"disambiguationData":[OSD([sQuery(id+"F2.wireOp",EDGE,"E2.top")])]});var subQ21=sQuery(id+"F0.wireOp",EDGE,"E0.top");var subQ22=makeQuery(id+"F1.opExtrude","SWEPT_FACE",FACE,{"disambiguationData":[OSD([subQ21])]});var subQ26=sQuery(id+"F0.wireOp",EDGE,"E0.left");var subQ28=sQuery(id+"F2.wireOp",EDGE,"E1.top");var subQ29=makeQuery(id+"F3.opExtrude","SWEPT_FACE",FACE,{"disambiguationData":[OSD([subQ28])]});var subQ32=makeQuery(id+"F3.boolean.opBoolean","MERGE",FACE,{"derivedFrom":[subQ22,subQ29,subQ18,subQ8]});var subQ33=makeQuery(id+"F5.boolean.opBoolean","SPLIT",FACE,{"disambiguationData":[TD([subQ9])],"derivedFrom":subQ32});var subQ34=makeQuery(id+"F12.opPattern","COPY",FACE,{"derivedFrom":subQ33,"instanceName":"1"});var subQ35=subQ34;var subQ36=makeQuery(id+"F15.opPattern","COPY",FACE,{"derivedFrom":subQ35,"instanceName":"1"});var subQ37=makeQuery(id+"F11.opExtrude","SWEPT_FACE",FACE,{"disambiguationData":[OSD([sQuery(id+"F10.wireOp",EDGE,"E13.left")])]});var subQ48=sQuery(id+"F20.wireOp",EDGE,"E26");var subQ49=sQuery(id+"F20.wireOp",EDGE,"E25");var subQ57=sQuery(id+"F4.wireOp",EDGE,"E4.bottom");var subQ58=sQuery(id+"F2.wireOp",EDGE,"E1.left");var subQ63=makeQuery(id+"F3.opExtrude","SWEPT_FACE",FACE,{"disambiguationData":[OSD([subQ58])]});var subQ65=makeQuery(id+"F5.boolean.opBoolean","SPLIT",FACE,{"disambiguationData":[TD([subQ63])],"derivedFrom":subQ32});var subQ66=makeQuery(id+"F12.opPattern","COPY",FACE,{"derivedFrom":subQ65,"instanceName":"1"});var subQ67=makeQuery(id+"F12.boolean.opBoolean","MERGE",FACE,{"derivedFrom":[subQ65,subQ66]});var subQ68=makeQuery(id+"F15.opPattern","COPY",FACE,{"derivedFrom":subQ67,"instanceName":"1"});var subQ83=makeQuery(id+"F15.opPattern","COPY",FACE,{"derivedFrom":subQ10,"instanceName":"1"});var subQ84=sQuery(id+"F22.wireOp",EDGE,"E42");var subQ85=sQuery(id+"F22.wireOp",EDGE,"E41");var subQ86=sQuery(id+"F22.wireOp",EDGE,"E39");var subQ87=sQuery(id+"F22.wireOp",EDGE,"E38");var subQ88=sQuery(id+"F22.wireOp",EDGE,"E37");var subQ89=sQuery(id+"F22.wireOp",EDGE,"E36");var subQ90=sQuery(id+"F22.wireOp",EDGE,"E35");var subQ91=makeQuery(id+"F23.opExtrude","CAP_FACE",FACE,{"disambiguationData":[OSD([subQ90,subQ89,subQ88,subQ87,subQ86,subQ85,subQ84])],"isStart":false});var subQ93=makeQuery(id+"F15.opPattern","COPY",FACE,{"derivedFrom":subQ33,"instanceName":"1"});var subQ103=sQuery(id+"F16.wireOp",EDGE,"E16.right");var subQ105=sQuery(id+"F16.wireOp",EDGE,"E16.top");var subQ112=makeQuery(id+"F5.opExtrude","SWEPT_EDGE",EDGE,{"disambiguationData":[OSD([subQ21,subQ28,subQ58,subQ57,subQ13])]});var subQ113=makeQuery(id+"F5.boolean.opBoolean","MERGE",EDGE,{"derivedFrom":[makeQuery(id+"F1.opExtrude","CAP_EDGE",EDGE,{"disambiguationData":[OSD([subQ26])],"isStart":false}),makeQuery(id+"F5.opExtrude","SWEPT_EDGE",EDGE,{"disambiguationData":[OSD([subQ57,subQ16])]})]});Q2=makeQuery(id+"F37.boolean.opBoolean","SPLIT",FACE,{"disambiguationData":[TD([subQ37])],"derivedFrom":makeQuery(id+"F33.boolean.opBoolean","SPLIT",FACE,{"disambiguationData":[TD([subQ83])],"derivedFrom":makeQuery(id+"F23.boolean.opBoolean","MERGE",FACE,{"derivedFrom":[makeQuery(id+"F21.boolean.opBoolean","MERGE",FACE,{"derivedFrom":[subQ33,subQ93,makeQuery(id+"F17.boolean.opBoolean","MERGE",FACE,{"derivedFrom":[subQ67,subQ68,makeQuery(id+"F15.boolean.opBoolean","MERGE",FACE,{"derivedFrom":[subQ35,subQ36]})],"fromTools":[makeQuery(id+"F17.opExtrude","CAP_FACE",FACE,{"disambiguationData":[OSD([sQuery(id+"F16.wireOp",EDGE,"E16.bottom"),subQ105,sQuery(id+"F16.wireOp",EDGE,"E16.left"),subQ103])],"isStart":false})]})],"fromTools":[makeQuery(id+"F21.opExtrude","SWEPT_FACE",FACE,{"disambiguationData":[OSD([subQ48]),TDD([makeQuery(id+"F20.imprint","IMPRINT",EDGE,{"disambiguationData":[TD([[makeQuery(id+"F20.imprint","INTERSECT",VERTEX,{"derivedFrom":[makeQuery(id+"F15.opPattern","COPY",EDGE,{"derivedFrom":subQ112,"instanceName":"1"}),subQ48]}),1.0],[makeQuery(id+"F20.imprint","INTERSECT",VERTEX,{"derivedFrom":[makeQuery(id+"F15.opPattern","COPY",EDGE,{"derivedFrom":subQ113,"instanceName":"1"}),subQ49,subQ48]}),-1.0]])],"derivedFrom":subQ48})])]}),makeQuery(id+"F21.opExtrude","SWEPT_FACE",FACE,{"disambiguationData":[OSD([subQ48]),TDD([makeQuery(id+"F20.imprint","IMPRINT",EDGE,{"disambiguationData":[TD([[makeQuery(id+"F20.imprint","INTERSECT",VERTEX,{"derivedFrom":[subQ112,subQ48]}),-1.0],[makeQuery(id+"F20.imprint","INTERSECT",VERTEX,{"derivedFrom":[subQ113,sQuery(id+"F20.wireOp",EDGE,"E19"),subQ48]}),1.0]])],"derivedFrom":subQ48})])]})]}),subQ7,subQ91]})})});}
            loft(context, id + "F39", {"operationType" : NewBodyOperationType.ADD, "sheetProfilesArray" : [{ "sheetProfileEntities" : qUnion([Q1]) }, { "sheetProfileEntities" : qUnion([Q2]) }]});
        }
        {
            var Q0;
            {var subQ0=makeQuery(id+"F11.boolean.opBoolean","MERGE",FACE,{"derivedFrom":[makeQuery(id+"F7.boolean.opBoolean","MERGE",FACE,{"derivedFrom":[makeQuery(id+"F5.opExtrude","CAP_FACE",FACE,{"disambiguationData":[OSD([sQuery(id+"F4.wireOp",EDGE,"E4.bottom"),sQuery(id+"F4.wireOp",EDGE,"E4.top"),sQuery(id+"F4.wireOp",EDGE,"E4.left"),sQuery(id+"F4.wireOp",EDGE,"E4.right")])],"isStart":false}),makeQuery(id+"F5.opExtrude","CAP_FACE",FACE,{"disambiguationData":[OSD([sQuery(id+"F4.wireOp",EDGE,"E5.bottom"),sQuery(id+"F4.wireOp",EDGE,"E5.top"),sQuery(id+"F4.wireOp",EDGE,"E5.left"),sQuery(id+"F4.wireOp",EDGE,"E5.right")])],"isStart":false}),makeQuery(id+"F5.opExtrude","CAP_FACE",FACE,{"disambiguationData":[OSD([sQuery(id+"F4.wireOp",EDGE,"E6.bottom"),sQuery(id+"F4.wireOp",EDGE,"E6.top"),sQuery(id+"F4.wireOp",EDGE,"E6.left"),sQuery(id+"F4.wireOp",EDGE,"E6.right")])],"isStart":false}),makeQuery(id+"F7.opExtrude","SWEPT_FACE",FACE,{"disambiguationData":[OSD([sQuery(id+"F6.wireOp",EDGE,"E7.bottom")])]})]}),makeQuery(id+"F11.opExtrude","SWEPT_FACE",FACE,{"disambiguationData":[OSD([sQuery(id+"F10.wireOp",EDGE,"E12.bottom")])]}),makeQuery(id+"F11.opExtrude","SWEPT_FACE",FACE,{"disambiguationData":[OSD([sQuery(id+"F10.wireOp",EDGE,"E13.top")])]}),makeQuery(id+"F11.opExtrude","SWEPT_FACE",FACE,{"disambiguationData":[OSD([sQuery(id+"F10.wireOp",EDGE,"E14.top")])]})]});var subQ1=makeQuery(id+"F12.boolean.opBoolean","MERGE",FACE,{"derivedFrom":[subQ0,makeQuery(id+"F12.opPattern","COPY",FACE,{"derivedFrom":subQ0,"instanceName":"1"})]});Q0=makeQuery(id+"F19.boolean.opBoolean","MERGE",FACE,{"derivedFrom":[makeQuery(id+"F15.boolean.opBoolean","MERGE",FACE,{"derivedFrom":[subQ1,makeQuery(id+"F15.opPattern","COPY",FACE,{"derivedFrom":subQ1,"instanceName":"1"})]}),makeQuery(id+"F19.opExtrude","CAP_FACE",FACE,{"disambiguationData":[OSD([sQuery(id+"F18.wireOp",EDGE,"E17.bottom"),sQuery(id+"F18.wireOp",EDGE,"E17.top"),sQuery(id+"F18.wireOp",EDGE,"E17.left"),sQuery(id+"F18.wireOp",EDGE,"E17.right")])],"isStart":true}),makeQuery(id+"F19.opExtrude","CAP_FACE",FACE,{"disambiguationData":[OSD([sQuery(id+"F18.wireOp",EDGE,"E18.bottom"),sQuery(id+"F18.wireOp",EDGE,"E18.top"),sQuery(id+"F18.wireOp",EDGE,"E18.left"),sQuery(id+"F18.wireOp",EDGE,"E18.right")])],"isStart":true})]});}
            var sketch = newSketch(context, id + "F40", { "sketchPlane" : qUnion([Q0])});
            skLineSegment(sketch, "E61.bottom", {"start": v(270, -490) * mm, "end": v(300, -490) * mm});
            skLineSegment(sketch, "E61.top", {"start": v(270, -290) * mm, "end": v(300, -290) * mm});
            skLineSegment(sketch, "E61.left", {"start": v(270, -490) * mm, "end": v(270, -290) * mm});
            skLineSegment(sketch, "E61.right", {"start": v(300, -490) * mm, "end": v(300, -290) * mm});
            skSolve(sketch);
        }
        {
            var Q0;
            Q0=makeQuery(id+"F40.imprint","IMPRINT",FACE,{"disambiguationData":[TD([[makeQuery(id+"F40.imprint","IMPRINT",EDGE,{"derivedFrom":sQuery(id+"F40.wireOp",EDGE,"E61.bottom")}),1.0]])]});
            extrude(context, id + "F41", {"entities" : qUnion([Q0]), "operationType" : NewBodyOperationType.REMOVE, "endBound" : BoundingType.UP_TO_NEXT, "oppositeDirection" : true, "depth" : 25 * mm, "offsetDistance" : 25 * mm});
        }
        {
            var Q0;
            {var subQ0=makeQuery(id+"F12.opPattern","COPY",FACE,{"derivedFrom":makeQuery(id+"F5.opExtrude","SWEPT_FACE",FACE,{"disambiguationData":[OSD([sQuery(id+"F4.wireOp",EDGE,"E6.top")])]}),"instanceName":"1"});var subQ1=makeQuery(id+"F11.opExtrude","SWEPT_FACE",FACE,{"disambiguationData":[OSD([sQuery(id+"F10.wireOp",EDGE,"E13.right")])]});var subQ2=makeQuery(id+"F12.boolean.opBoolean","MERGE",FACE,{"derivedFrom":[subQ1,makeQuery(id+"F12.opPattern","COPY",FACE,{"derivedFrom":subQ1,"instanceName":"1"})]});Q0=makeQuery(id+"F41.boolean.opBoolean","MERGE",FACE,{"derivedFrom":[subQ2,makeQuery(id+"F15.opPattern","COPY",FACE,{"derivedFrom":subQ2,"instanceName":"1"}),makeQuery(id+"F15.boolean.opBoolean","MERGE",FACE,{"derivedFrom":[subQ0,makeQuery(id+"F15.opPattern","COPY",FACE,{"derivedFrom":subQ0,"instanceName":"1"})]})],"fromTools":[makeQuery(id+"F41.opExtrude","SWEPT_FACE",FACE,{"disambiguationData":[OSD([sQuery(id+"F40.wireOp",EDGE,"E61.bottom")])]})]});}
            var sketch = newSketch(context, id + "F42", { "sketchPlane" : qUnion([Q0])});
            skLineSegment(sketch, "E62.bottom", {"start": v(-375, 170) * mm, "end": v(-345, 170) * mm});
            skLineSegment(sketch, "E62.top", {"start": v(-375, 140) * mm, "end": v(-345, 140) * mm});
            skLineSegment(sketch, "E62.left", {"start": v(-375, 170) * mm, "end": v(-375, 140) * mm});
            skLineSegment(sketch, "E62.right", {"start": v(-345, 170) * mm, "end": v(-345, 140) * mm});
            skLineSegment(sketch, "E63.bottom", {"start": v(-195, 170) * mm, "end": v(-225, 170) * mm});
            skLineSegment(sketch, "E63.top", {"start": v(-195, 140) * mm, "end": v(-225, 140) * mm});
            skLineSegment(sketch, "E63.left", {"start": v(-195, 170) * mm, "end": v(-195, 140) * mm});
            skLineSegment(sketch, "E63.right", {"start": v(-225, 170) * mm, "end": v(-225, 140) * mm});
            skSolve(sketch);
        }
        {
            var Q0;
            Q0 = qSketchRegion(id + "F42", true);
            extrude(context, id + "F43", {"entities" : qUnion([Q0]), "operationType" : NewBodyOperationType.ADD, "endBound" : BoundingType.UP_TO_NEXT, "depth" : 25 * mm, "offsetDistance" : 25 * mm});
        }
        {
            var Q0;
            {var subQ16=makeQuery(id+"F11.opExtrude","SWEPT_FACE",FACE,{"disambiguationData":[OSD([sQuery(id+"F10.wireOp",EDGE,"E14.left")])]});var subQ20=makeQuery(id+"F1.opExtrude","SWEPT_FACE",FACE,{"disambiguationData":[OSD([sQuery(id+"F0.wireOp",EDGE,"E0.top")])]});var subQ22=sQuery(id+"F4.wireOp",EDGE,"E5.bottom");var subQ23=makeQuery(id+"F5.opExtrude","SWEPT_FACE",FACE,{"disambiguationData":[OSD([subQ22])]});var subQ59=makeQuery(id+"F12.opPattern","COPY",FACE,{"derivedFrom":subQ23,"instanceName":"1"});var subQ60=makeQuery(id+"F12.boolean.opBoolean","MERGE",FACE,{"derivedFrom":[subQ16,makeQuery(id+"F12.opPattern","COPY",FACE,{"derivedFrom":subQ16,"instanceName":"1"})]});Q0=makeQuery(id+"F43.boolean.opBoolean","SPLIT",FACE,{"disambiguationData":[TD([subQ20])],"derivedFrom":makeQuery(id+"F41.boolean.opBoolean","MERGE",FACE,{"derivedFrom":[subQ60,makeQuery(id+"F15.opPattern","COPY",FACE,{"derivedFrom":subQ60,"instanceName":"1"}),makeQuery(id+"F15.boolean.opBoolean","MERGE",FACE,{"derivedFrom":[subQ59,makeQuery(id+"F15.opPattern","COPY",FACE,{"derivedFrom":subQ59,"instanceName":"1"})]})],"fromTools":[makeQuery(id+"F41.opExtrude","SWEPT_FACE",FACE,{"disambiguationData":[OSD([sQuery(id+"F40.wireOp",EDGE,"E61.top")])]})]})});}
            var sketch = newSketch(context, id + "F44", { "sketchPlane" : qUnion([Q0])});
            skPoint(sketch, "E64", {"position": v(285, 90) * mm});
            skPoint(sketch, "E65", {"position": v(285, 50) * mm});
            skSolve(sketch);
        }
        {
            var Q0;
            Q0=sQuery(id+"F44.wireOp",VERTEX,"E65");
            var Q1;
            Q1=sQuery(id+"F44.wireOp",VERTEX,"E64");
            var Q2;
            Q2=makeQuery(id+"F1.opExtrude","SWEPT_BODY",BODY,{"disambiguationData":[OSD([sQuery(id+"F0.wireOp",EDGE,"E0.bottom"),sQuery(id+"F0.wireOp",EDGE,"E0.top"),sQuery(id+"F0.wireOp",EDGE,"E0.left"),sQuery(id+"F0.wireOp",EDGE,"E0.right")])]});
            hole(context, id + "F45", {"style" : HoleStyle.SIMPLE, "endStyle" : HoleEndStyle.BLIND, "holeDiameter" : 10 * mm, "majorDiameter" : 5 * mm, "holeDepth" : 30 * mm, "isTappedThrough" : true, "tappedDepth" : 12 * mm, "tapClearance" : 3, "locations" : qUnion([Q0, Q1]), "scope" : qUnion([Q2])});
        }
        {
            var Q1;
            Q1=makeQuery(id+"F23.opExtrude","SWEPT_FACE",FACE,{"disambiguationData":[OSD([sQuery(id+"F22.wireOp",EDGE,"E27")])]});
            var Q2;
            Q2=makeQuery(id+"F29.opLoft","SWEPT_FACE",FACE,{"disambiguationData":[OSD([sQuery(id+"F0.wireOp",EDGE,"E0.top"),sQuery(id+"F2.wireOp",EDGE,"E1.top"),sQuery(id+"F2.wireOp",EDGE,"E1.left"),sQuery(id+"F4.wireOp",EDGE,"E4.bottom"),sQuery(id+"F4.wireOp",EDGE,"E4.right"),sQuery(id+"F10.wireOp",EDGE,"E12.bottom"),sQuery(id+"F10.wireOp",EDGE,"E12.top"),sQuery(id+"F10.wireOp",EDGE,"E12.left"),sQuery(id+"F20.wireOp",EDGE,"E20"),sQuery(id+"F20.wireOp",EDGE,"E21"),sQuery(id+"F20.wireOp",EDGE,"E22"),sQuery(id+"F22.wireOp",EDGE,"E31"),sQuery(id+"F28.wireOp",EDGE,"E49"),sQuery(id+"F28.wireOp",EDGE,"E51"),sQuery(id+"F28.wireOp",EDGE,"E52")])]});
            loft(context, id + "F46", {"operationType" : NewBodyOperationType.ADD, "sheetProfilesArray" : [{ "sheetProfileEntities" : qUnion([Q1]) }, { "sheetProfileEntities" : qUnion([Q2]) }]});
        }
        {
            var Q1;
            Q1=makeQuery(id+"F31.opLoft","SWEPT_FACE",FACE,{"disambiguationData":[OSD([sQuery(id+"F0.wireOp",EDGE,"E0.top"),sQuery(id+"F2.wireOp",EDGE,"E1.top"),sQuery(id+"F2.wireOp",EDGE,"E1.left"),sQuery(id+"F4.wireOp",EDGE,"E4.bottom"),sQuery(id+"F4.wireOp",EDGE,"E4.right"),sQuery(id+"F10.wireOp",EDGE,"E12.bottom"),sQuery(id+"F10.wireOp",EDGE,"E12.top"),sQuery(id+"F10.wireOp",EDGE,"E12.left"),sQuery(id+"F20.wireOp",EDGE,"E22"),sQuery(id+"F20.wireOp",EDGE,"E23"),sQuery(id+"F20.wireOp",EDGE,"E24"),sQuery(id+"F22.wireOp",EDGE,"E39"),sQuery(id+"F30.wireOp",EDGE,"E53"),sQuery(id+"F30.wireOp",EDGE,"E54"),sQuery(id+"F30.wireOp",EDGE,"E56")])]});
            var Q2;
            Q2=makeQuery(id+"F23.opExtrude","SWEPT_FACE",FACE,{"disambiguationData":[OSD([sQuery(id+"F22.wireOp",EDGE,"E35")])]});
            loft(context, id + "F47", {"operationType" : NewBodyOperationType.ADD, "sheetProfilesArray" : [{ "sheetProfileEntities" : qUnion([Q1]) }, { "sheetProfileEntities" : qUnion([Q2]) }]});
        }
        {
            var Q0;
            {var subQ0=makeQuery(id+"F3.boolean.opBoolean","MERGE",FACE,{"derivedFrom":[makeQuery(id+"F1.opExtrude","SWEPT_FACE",FACE,{"disambiguationData":[OSD([sQuery(id+"F0.wireOp",EDGE,"E0.bottom")])]}),makeQuery(id+"F3.opExtrude","SWEPT_FACE",FACE,{"disambiguationData":[OSD([sQuery(id+"F2.wireOp",EDGE,"E1.bottom")])]}),makeQuery(id+"F3.opExtrude","SWEPT_FACE",FACE,{"disambiguationData":[OSD([sQuery(id+"F2.wireOp",EDGE,"E2.bottom")])]}),makeQuery(id+"F3.opExtrude","SWEPT_FACE",FACE,{"disambiguationData":[OSD([sQuery(id+"F2.wireOp",EDGE,"E3.bottom")])]})]});var subQ1=makeQuery(id+"F12.boolean.opBoolean","MERGE",FACE,{"derivedFrom":[subQ0,makeQuery(id+"F12.opPattern","COPY",FACE,{"derivedFrom":subQ0,"instanceName":"1"})]});Q0=makeQuery(id+"F23.boolean.opBoolean","MERGE",FACE,{"derivedFrom":[makeQuery(id+"F15.boolean.opBoolean","MERGE",FACE,{"derivedFrom":[subQ1,makeQuery(id+"F15.opPattern","COPY",FACE,{"derivedFrom":subQ1,"instanceName":"1"})]}),makeQuery(id+"F23.opExtrude","CAP_FACE",FACE,{"disambiguationData":[OSD([sQuery(id+"F22.wireOp",EDGE,"E27"),sQuery(id+"F22.wireOp",EDGE,"E28"),sQuery(id+"F22.wireOp",EDGE,"E29"),sQuery(id+"F22.wireOp",EDGE,"E30"),sQuery(id+"F22.wireOp",EDGE,"E31"),sQuery(id+"F22.wireOp",EDGE,"E33"),sQuery(id+"F22.wireOp",EDGE,"E34")])],"isStart":true}),makeQuery(id+"F23.opExtrude","CAP_FACE",FACE,{"disambiguationData":[OSD([sQuery(id+"F22.wireOp",EDGE,"E35"),sQuery(id+"F22.wireOp",EDGE,"E36"),sQuery(id+"F22.wireOp",EDGE,"E37"),sQuery(id+"F22.wireOp",EDGE,"E38"),sQuery(id+"F22.wireOp",EDGE,"E39"),sQuery(id+"F22.wireOp",EDGE,"E41"),sQuery(id+"F22.wireOp",EDGE,"E42")])],"isStart":true})]});}
            var sketch = newSketch(context, id + "F48", { "sketchPlane" : qUnion([Q0])});
            skLineSegment(sketch, "E66.bottom", {"start": v(300, 360) * mm, "end": v(540, 360) * mm});
            skLineSegment(sketch, "E66.top", {"start": v(300, 390) * mm, "end": v(540, 390) * mm});
            skLineSegment(sketch, "E66.left", {"start": v(300, 360) * mm, "end": v(300, 390) * mm});
            skLineSegment(sketch, "E66.right", {"start": v(540, 360) * mm, "end": v(540, 390) * mm});
            skLineSegment(sketch, "E67.bottom", {"start": v(30, 390) * mm, "end": v(270, 390) * mm});
            skLineSegment(sketch, "E67.top", {"start": v(30, 360) * mm, "end": v(270, 360) * mm});
            skLineSegment(sketch, "E67.left", {"start": v(30, 390) * mm, "end": v(30, 360) * mm});
            skLineSegment(sketch, "E67.right", {"start": v(270, 390) * mm, "end": v(270, 360) * mm});
            skSolve(sketch);
        }
        {
            var Q0;
            Q0 = qSketchRegion(id + "F48", true);
            extrude(context, id + "F49", {"entities" : qUnion([Q0]), "operationType" : NewBodyOperationType.REMOVE, "endBound" : BoundingType.UP_TO_NEXT, "oppositeDirection" : true, "depth" : 25 * mm, "offsetDistance" : 25 * mm});
        }
        {
            var Q0;
            {var subQ0=makeQuery(id+"F3.boolean.opBoolean","MERGE",FACE,{"derivedFrom":[makeQuery(id+"F1.opExtrude","SWEPT_FACE",FACE,{"disambiguationData":[OSD([sQuery(id+"F0.wireOp",EDGE,"E0.bottom")])]}),makeQuery(id+"F3.opExtrude","SWEPT_FACE",FACE,{"disambiguationData":[OSD([sQuery(id+"F2.wireOp",EDGE,"E1.bottom")])]}),makeQuery(id+"F3.opExtrude","SWEPT_FACE",FACE,{"disambiguationData":[OSD([sQuery(id+"F2.wireOp",EDGE,"E2.bottom")])]}),makeQuery(id+"F3.opExtrude","SWEPT_FACE",FACE,{"disambiguationData":[OSD([sQuery(id+"F2.wireOp",EDGE,"E3.bottom")])]})]});var subQ1=makeQuery(id+"F12.boolean.opBoolean","MERGE",FACE,{"derivedFrom":[subQ0,makeQuery(id+"F12.opPattern","COPY",FACE,{"derivedFrom":subQ0,"instanceName":"1"})]});Q0=makeQuery(id+"F23.boolean.opBoolean","MERGE",FACE,{"derivedFrom":[makeQuery(id+"F15.boolean.opBoolean","MERGE",FACE,{"derivedFrom":[subQ1,makeQuery(id+"F15.opPattern","COPY",FACE,{"derivedFrom":subQ1,"instanceName":"1"})]}),makeQuery(id+"F23.opExtrude","CAP_FACE",FACE,{"disambiguationData":[OSD([sQuery(id+"F22.wireOp",EDGE,"E27"),sQuery(id+"F22.wireOp",EDGE,"E28"),sQuery(id+"F22.wireOp",EDGE,"E29"),sQuery(id+"F22.wireOp",EDGE,"E30"),sQuery(id+"F22.wireOp",EDGE,"E31"),sQuery(id+"F22.wireOp",EDGE,"E33"),sQuery(id+"F22.wireOp",EDGE,"E34")])],"isStart":true}),makeQuery(id+"F23.opExtrude","CAP_FACE",FACE,{"disambiguationData":[OSD([sQuery(id+"F22.wireOp",EDGE,"E35"),sQuery(id+"F22.wireOp",EDGE,"E36"),sQuery(id+"F22.wireOp",EDGE,"E37"),sQuery(id+"F22.wireOp",EDGE,"E38"),sQuery(id+"F22.wireOp",EDGE,"E39"),sQuery(id+"F22.wireOp",EDGE,"E41"),sQuery(id+"F22.wireOp",EDGE,"E42")])],"isStart":true})]});}
            var sketch = newSketch(context, id + "F50", { "sketchPlane" : qUnion([Q0])});
            skLineSegment(sketch, "E68.bottom", {"start": v(300, 490) * mm, "end": v(540, 490) * mm});
            skLineSegment(sketch, "E68.top", {"start": v(300, 520) * mm, "end": v(540, 520) * mm});
            skLineSegment(sketch, "E68.left", {"start": v(300, 490) * mm, "end": v(300, 520) * mm});
            skLineSegment(sketch, "E68.right", {"start": v(540, 490) * mm, "end": v(540, 520) * mm});
            skLineSegment(sketch, "E69.bottom", {"start": v(30, 520) * mm, "end": v(270, 520) * mm});
            skLineSegment(sketch, "E69.top", {"start": v(30, 490) * mm, "end": v(270, 490) * mm});
            skLineSegment(sketch, "E69.left", {"start": v(30, 520) * mm, "end": v(30, 490) * mm});
            skLineSegment(sketch, "E69.right", {"start": v(270, 520) * mm, "end": v(270, 490) * mm});
            skLineSegment(sketch, "E70.bottom", {"start": v(30, 290) * mm, "end": v(270, 290) * mm});
            skLineSegment(sketch, "E70.top", {"start": v(30, 260) * mm, "end": v(270, 260) * mm});
            skLineSegment(sketch, "E70.left", {"start": v(30, 290) * mm, "end": v(30, 260) * mm});
            skLineSegment(sketch, "E70.right", {"start": v(270, 290) * mm, "end": v(270, 260) * mm});
            skLineSegment(sketch, "E71.bottom", {"start": v(300, 290) * mm, "end": v(540, 290) * mm});
            skLineSegment(sketch, "E71.top", {"start": v(300, 260) * mm, "end": v(540, 260) * mm});
            skLineSegment(sketch, "E71.left", {"start": v(300, 290) * mm, "end": v(300, 260) * mm});
            skLineSegment(sketch, "E71.right", {"start": v(540, 290) * mm, "end": v(540, 260) * mm});
            skSolve(sketch);
        }
        {
            var Q0;
            Q0 = qSketchRegion(id + "F50", true);
            extrude(context, id + "F51", {"entities" : qUnion([Q0]), "operationType" : NewBodyOperationType.ADD, "oppositeDirection" : true, "depth" : 30 * mm, "offsetDistance" : 25 * mm});
        }
        {
            var Q0;
            {var subQ0=makeQuery(id+"F11.boolean.opBoolean","MERGE",FACE,{"derivedFrom":[makeQuery(id+"F7.boolean.opBoolean","MERGE",FACE,{"derivedFrom":[makeQuery(id+"F5.opExtrude","CAP_FACE",FACE,{"disambiguationData":[OSD([sQuery(id+"F4.wireOp",EDGE,"E4.bottom"),sQuery(id+"F4.wireOp",EDGE,"E4.top"),sQuery(id+"F4.wireOp",EDGE,"E4.left"),sQuery(id+"F4.wireOp",EDGE,"E4.right")])],"isStart":false}),makeQuery(id+"F5.opExtrude","CAP_FACE",FACE,{"disambiguationData":[OSD([sQuery(id+"F4.wireOp",EDGE,"E5.bottom"),sQuery(id+"F4.wireOp",EDGE,"E5.top"),sQuery(id+"F4.wireOp",EDGE,"E5.left"),sQuery(id+"F4.wireOp",EDGE,"E5.right")])],"isStart":false}),makeQuery(id+"F5.opExtrude","CAP_FACE",FACE,{"disambiguationData":[OSD([sQuery(id+"F4.wireOp",EDGE,"E6.bottom"),sQuery(id+"F4.wireOp",EDGE,"E6.top"),sQuery(id+"F4.wireOp",EDGE,"E6.left"),sQuery(id+"F4.wireOp",EDGE,"E6.right")])],"isStart":false}),makeQuery(id+"F7.opExtrude","SWEPT_FACE",FACE,{"disambiguationData":[OSD([sQuery(id+"F6.wireOp",EDGE,"E7.bottom")])]})]}),makeQuery(id+"F11.opExtrude","SWEPT_FACE",FACE,{"disambiguationData":[OSD([sQuery(id+"F10.wireOp",EDGE,"E12.bottom")])]}),makeQuery(id+"F11.opExtrude","SWEPT_FACE",FACE,{"disambiguationData":[OSD([sQuery(id+"F10.wireOp",EDGE,"E13.top")])]}),makeQuery(id+"F11.opExtrude","SWEPT_FACE",FACE,{"disambiguationData":[OSD([sQuery(id+"F10.wireOp",EDGE,"E14.top")])]})]});var subQ1=makeQuery(id+"F12.boolean.opBoolean","MERGE",FACE,{"derivedFrom":[subQ0,makeQuery(id+"F12.opPattern","COPY",FACE,{"derivedFrom":subQ0,"instanceName":"1"})]});Q0=makeQuery(id+"F43.boolean.opBoolean","MERGE",FACE,{"derivedFrom":[makeQuery(id+"F19.boolean.opBoolean","MERGE",FACE,{"derivedFrom":[makeQuery(id+"F15.boolean.opBoolean","MERGE",FACE,{"derivedFrom":[subQ1,makeQuery(id+"F15.opPattern","COPY",FACE,{"derivedFrom":subQ1,"instanceName":"1"})]}),makeQuery(id+"F19.opExtrude","CAP_FACE",FACE,{"disambiguationData":[OSD([sQuery(id+"F18.wireOp",EDGE,"E17.bottom"),sQuery(id+"F18.wireOp",EDGE,"E17.top"),sQuery(id+"F18.wireOp",EDGE,"E17.left"),sQuery(id+"F18.wireOp",EDGE,"E17.right")])],"isStart":true}),makeQuery(id+"F19.opExtrude","CAP_FACE",FACE,{"disambiguationData":[OSD([sQuery(id+"F18.wireOp",EDGE,"E18.bottom"),sQuery(id+"F18.wireOp",EDGE,"E18.top"),sQuery(id+"F18.wireOp",EDGE,"E18.left"),sQuery(id+"F18.wireOp",EDGE,"E18.right")])],"isStart":true})]}),makeQuery(id+"F43.opExtrude","SWEPT_FACE",FACE,{"disambiguationData":[OSD([sQuery(id+"F42.wireOp",EDGE,"E62.bottom")])]}),makeQuery(id+"F43.opExtrude","SWEPT_FACE",FACE,{"disambiguationData":[OSD([sQuery(id+"F42.wireOp",EDGE,"E63.bottom")])]})]});}
            var sketch = newSketch(context, id + "F52", { "sketchPlane" : qUnion([Q0])});
            skCircle(sketch, "E72", {"center": v(17.5, -502.5) * mm, "radius": 15 * mm});
            skCircle(sketch, "E73", {"center": v(552.5, -502.5) * mm, "radius": 15 * mm});
            skSolve(sketch);
        }
        {
            var Q0;
            Q0 = qSketchRegion(id + "F52", true);
            extrude(context, id + "F53", {"entities" : qUnion([Q0]), "operationType" : NewBodyOperationType.ADD, "depth" : 50 * mm, "offsetDistance" : 25 * mm});
        }
        {
            var Q0;
            Q0=makeQuery(id+"F53.opExtrude","CAP_EDGE",EDGE,{"disambiguationData":[OSD([sQuery(id+"F52.wireOp",EDGE,"E73")])],"isStart":false});
            var Q1;
            Q1=makeQuery(id+"F53.opExtrude","CAP_EDGE",EDGE,{"disambiguationData":[OSD([sQuery(id+"F52.wireOp",EDGE,"E72")])],"isStart":false});
            fillet(context, id + "F54", {"entities" : qUnion([Q0, Q1]), "radius" : 5 * mm, "tangentPropagation" : true, "allowEdgeOverflow" : false});
        }
        {
            var Q0;
            {var subQ0=makeQuery(id+"F3.boolean.opBoolean","MERGE",FACE,{"derivedFrom":[makeQuery(id+"F1.opExtrude","SWEPT_FACE",FACE,{"disambiguationData":[OSD([sQuery(id+"F0.wireOp",EDGE,"E0.bottom")])]}),makeQuery(id+"F3.opExtrude","SWEPT_FACE",FACE,{"disambiguationData":[OSD([sQuery(id+"F2.wireOp",EDGE,"E1.bottom")])]}),makeQuery(id+"F3.opExtrude","SWEPT_FACE",FACE,{"disambiguationData":[OSD([sQuery(id+"F2.wireOp",EDGE,"E2.bottom")])]}),makeQuery(id+"F3.opExtrude","SWEPT_FACE",FACE,{"disambiguationData":[OSD([sQuery(id+"F2.wireOp",EDGE,"E3.bottom")])]})]});var subQ1=makeQuery(id+"F12.boolean.opBoolean","MERGE",FACE,{"derivedFrom":[subQ0,makeQuery(id+"F12.opPattern","COPY",FACE,{"derivedFrom":subQ0,"instanceName":"1"})]});Q0=makeQuery(id+"F51.boolean.opBoolean","MERGE",FACE,{"derivedFrom":[makeQuery(id+"F23.boolean.opBoolean","MERGE",FACE,{"derivedFrom":[makeQuery(id+"F15.boolean.opBoolean","MERGE",FACE,{"derivedFrom":[subQ1,makeQuery(id+"F15.opPattern","COPY",FACE,{"derivedFrom":subQ1,"instanceName":"1"})]}),makeQuery(id+"F23.opExtrude","CAP_FACE",FACE,{"disambiguationData":[OSD([sQuery(id+"F22.wireOp",EDGE,"E27"),sQuery(id+"F22.wireOp",EDGE,"E28"),sQuery(id+"F22.wireOp",EDGE,"E29"),sQuery(id+"F22.wireOp",EDGE,"E30"),sQuery(id+"F22.wireOp",EDGE,"E31"),sQuery(id+"F22.wireOp",EDGE,"E33"),sQuery(id+"F22.wireOp",EDGE,"E34")])],"isStart":true}),makeQuery(id+"F23.opExtrude","CAP_FACE",FACE,{"disambiguationData":[OSD([sQuery(id+"F22.wireOp",EDGE,"E35"),sQuery(id+"F22.wireOp",EDGE,"E36"),sQuery(id+"F22.wireOp",EDGE,"E37"),sQuery(id+"F22.wireOp",EDGE,"E38"),sQuery(id+"F22.wireOp",EDGE,"E39"),sQuery(id+"F22.wireOp",EDGE,"E41"),sQuery(id+"F22.wireOp",EDGE,"E42")])],"isStart":true})]}),makeQuery(id+"F51.opExtrude","CAP_FACE",FACE,{"disambiguationData":[OSD([sQuery(id+"F50.wireOp",EDGE,"E68.bottom"),sQuery(id+"F50.wireOp",EDGE,"E68.top"),sQuery(id+"F50.wireOp",EDGE,"E68.left"),sQuery(id+"F50.wireOp",EDGE,"E68.right")])],"isStart":true}),makeQuery(id+"F51.opExtrude","CAP_FACE",FACE,{"disambiguationData":[OSD([sQuery(id+"F50.wireOp",EDGE,"E69.bottom"),sQuery(id+"F50.wireOp",EDGE,"E69.top"),sQuery(id+"F50.wireOp",EDGE,"E69.left"),sQuery(id+"F50.wireOp",EDGE,"E69.right")])],"isStart":true}),makeQuery(id+"F51.opExtrude","CAP_FACE",FACE,{"disambiguationData":[OSD([sQuery(id+"F50.wireOp",EDGE,"E70.bottom"),sQuery(id+"F50.wireOp",EDGE,"E70.top"),sQuery(id+"F50.wireOp",EDGE,"E70.left"),sQuery(id+"F50.wireOp",EDGE,"E70.right")])],"isStart":true}),makeQuery(id+"F51.opExtrude","CAP_FACE",FACE,{"disambiguationData":[OSD([sQuery(id+"F50.wireOp",EDGE,"E71.bottom"),sQuery(id+"F50.wireOp",EDGE,"E71.top"),sQuery(id+"F50.wireOp",EDGE,"E71.left"),sQuery(id+"F50.wireOp",EDGE,"E71.right")])],"isStart":true})]});}
            var sketch = newSketch(context, id + "F55", { "sketchPlane" : qUnion([Q0])});
            skLineSegment(sketch, "E74.bottom", {"start": v(135, 520) * mm, "end": v(165, 520) * mm});
            skLineSegment(sketch, "E74.top", {"start": v(135, 720) * mm, "end": v(165, 720) * mm});
            skLineSegment(sketch, "E74.left", {"start": v(135, 520) * mm, "end": v(135, 720) * mm});
            skLineSegment(sketch, "E74.right", {"start": v(165, 520) * mm, "end": v(165, 720) * mm});
            skLineSegment(sketch, "E75.bottom", {"start": v(405, 520) * mm, "end": v(435, 520) * mm});
            skLineSegment(sketch, "E75.top", {"start": v(405, 720) * mm, "end": v(435, 720) * mm});
            skLineSegment(sketch, "E75.left", {"start": v(405, 520) * mm, "end": v(405, 720) * mm});
            skLineSegment(sketch, "E75.right", {"start": v(435, 520) * mm, "end": v(435, 720) * mm});
            skSolve(sketch);
        }
        {
            var Q0;
            Q0=makeQuery(id+"F55.imprint","IMPRINT",FACE,{"disambiguationData":[TD([[makeQuery(id+"F55.imprint","IMPRINT",EDGE,{"derivedFrom":sQuery(id+"F55.wireOp",EDGE,"E74.bottom")}),1.0]])]});
            var Q1;
            Q1=makeQuery(id+"F55.imprint","IMPRINT",FACE,{"disambiguationData":[TD([[makeQuery(id+"F55.imprint","IMPRINT",EDGE,{"derivedFrom":sQuery(id+"F55.wireOp",EDGE,"E75.bottom")}),1.0]])]});
            extrude(context, id + "F56", {"entities" : qUnion([Q0, Q1]), "operationType" : NewBodyOperationType.ADD, "oppositeDirection" : true, "depth" : 30 * mm, "offsetDistance" : 25 * mm});
        }
        {
            var Q0;
            Q0=makeQuery(id+"F15.opPattern","COPY",FACE,{"derivedFrom":makeQuery(id+"F9.boolean.opBoolean","MERGE",FACE,{"derivedFrom":[makeQuery(id+"F7.boolean.opBoolean","MERGE",FACE,{"derivedFrom":[makeQuery(id+"F5.boolean.opBoolean","MERGE",FACE,{"derivedFrom":[makeQuery(id+"F1.opExtrude","SWEPT_FACE",FACE,{"disambiguationData":[OSD([sQuery(id+"F0.wireOp",EDGE,"E0.left")])]}),makeQuery(id+"F5.opExtrude","SWEPT_FACE",FACE,{"disambiguationData":[OSD([sQuery(id+"F4.wireOp",EDGE,"E4.left")])]}),makeQuery(id+"F5.opExtrude","SWEPT_FACE",FACE,{"disambiguationData":[OSD([sQuery(id+"F4.wireOp",EDGE,"E5.right")])]}),makeQuery(id+"F5.opExtrude","SWEPT_FACE",FACE,{"disambiguationData":[OSD([sQuery(id+"F4.wireOp",EDGE,"E6.left")])]})]}),makeQuery(id+"F7.opExtrude","SWEPT_FACE",FACE,{"disambiguationData":[OSD([sQuery(id+"F6.wireOp",EDGE,"E7.right")])]})]}),makeQuery(id+"F9.opExtrude","CAP_FACE",FACE,{"disambiguationData":[OSD([sQuery(id+"F8.wireOp",EDGE,"E8"),sQuery(id+"F8.wireOp",EDGE,"E9"),sQuery(id+"F8.wireOp",EDGE,"E10"),sQuery(id+"F8.wireOp",EDGE,"E11")])],"isStart":true})]}),"instanceName":"1"});
            var sketch = newSketch(context, id + "F57", { "sketchPlane" : qUnion([Q0])});
            skLineSegment(sketch, "E76.bottom", {"start": v(-260, 170) * mm, "end": v(0, 170) * mm});
            skLineSegment(sketch, "E76.top", {"start": v(-260, 30) * mm, "end": v(0, 30) * mm});
            skLineSegment(sketch, "E76.left", {"start": v(-260, 170) * mm, "end": v(-260, 30) * mm});
            skLineSegment(sketch, "E76.right", {"start": v(0, 170) * mm, "end": v(0, 30) * mm});
            skSolve(sketch);
        }
        {
            var Q0;
            Q0=makeQuery(id+"F57.imprint","IMPRINT",FACE,{"disambiguationData":[TD([[makeQuery(id+"F57.imprint","IMPRINT",EDGE,{"derivedFrom":sQuery(id+"F57.wireOp",EDGE,"E76.bottom")}),-1.0]])]});
            var Q1;
            {var subQ1=makeQuery(id+"F15.opPattern","COPY",EDGE,{"derivedFrom":makeQuery(id+"F9.opExtrude","CAP_EDGE",EDGE,{"disambiguationData":[OSD([sQuery(id+"F8.wireOp",EDGE,"E8")])],"isStart":true}),"instanceName":"1"});Q1=makeQuery(id+"F57.imprint","IMPRINT",FACE,{"disambiguationData":[TD([[makeQuery(id+"F57.imprint","IMPRINT",EDGE,{"derivedFrom":subQ1}),-1.0]])]});}
            var Q2;
            {var subQ3=makeQuery(id+"F15.opPattern","COPY",EDGE,{"derivedFrom":makeQuery(id+"F9.opExtrude","CAP_EDGE",EDGE,{"disambiguationData":[OSD([sQuery(id+"F8.wireOp",EDGE,"E9")])],"isStart":true}),"instanceName":"1"});Q2=makeQuery(id+"F57.imprint","IMPRINT",FACE,{"disambiguationData":[TD([[makeQuery(id+"F57.imprint","IMPRINT",EDGE,{"derivedFrom":subQ3}),-1.0]])]});}
            extrude(context, id + "F58", {"entities" : qUnion([Q0, Q1, Q2]), "operationType" : NewBodyOperationType.REMOVE, "endBound" : BoundingType.THROUGH_ALL, "oppositeDirection" : true, "depth" : 25 * mm, "offsetDistance" : 25 * mm});
        }
        {
            var Q0;
            Q0=makeQuery(id+"F15.opPattern","COPY",FACE,{"derivedFrom":makeQuery(id+"F9.boolean.opBoolean","MERGE",FACE,{"derivedFrom":[makeQuery(id+"F7.boolean.opBoolean","MERGE",FACE,{"derivedFrom":[makeQuery(id+"F5.boolean.opBoolean","MERGE",FACE,{"derivedFrom":[makeQuery(id+"F1.opExtrude","SWEPT_FACE",FACE,{"disambiguationData":[OSD([sQuery(id+"F0.wireOp",EDGE,"E0.left")])]}),makeQuery(id+"F5.opExtrude","SWEPT_FACE",FACE,{"disambiguationData":[OSD([sQuery(id+"F4.wireOp",EDGE,"E4.left")])]}),makeQuery(id+"F5.opExtrude","SWEPT_FACE",FACE,{"disambiguationData":[OSD([sQuery(id+"F4.wireOp",EDGE,"E5.right")])]}),makeQuery(id+"F5.opExtrude","SWEPT_FACE",FACE,{"disambiguationData":[OSD([sQuery(id+"F4.wireOp",EDGE,"E6.left")])]})]}),makeQuery(id+"F7.opExtrude","SWEPT_FACE",FACE,{"disambiguationData":[OSD([sQuery(id+"F6.wireOp",EDGE,"E7.right")])]})]}),makeQuery(id+"F9.opExtrude","CAP_FACE",FACE,{"disambiguationData":[OSD([sQuery(id+"F8.wireOp",EDGE,"E8"),sQuery(id+"F8.wireOp",EDGE,"E9"),sQuery(id+"F8.wireOp",EDGE,"E10"),sQuery(id+"F8.wireOp",EDGE,"E11")])],"isStart":true})]}),"instanceName":"1"});
            var sketch = newSketch(context, id + "F59", { "sketchPlane" : qUnion([Q0])});
            skLineSegment(sketch, "E77", {"start": v(-260, 170) * mm, "end": v(-110, 170) * mm});
            skLineSegment(sketch, "E78", {"start": v(0, 60) * mm, "end": v(0, 30) * mm});
            skLineSegment(sketch, "E79", {"start": v(0, 30) * mm, "end": v(-30, 30) * mm});
            skLineSegment(sketch, "E80", {"start": v(-30, 30) * mm, "end": v(-30, 47.57) * mm});
            skLineSegment(sketch, "E81", {"start": v(-122.43, 140) * mm, "end": v(-260, 140) * mm});
            skLineSegment(sketch, "E82", {"start": v(-260, 140) * mm, "end": v(-260, 170) * mm});
            skLineSegment(sketch, "E83", {"start": v(-122.43, 140) * mm, "end": v(-30, 47.57) * mm});
            skLineSegment(sketch, "E84", {"start": v(-110, 170) * mm, "end": v(0, 60) * mm});
            skSolve(sketch);
        }
        {
            var Q0;
            Q0=makeQuery(id+"F59.imprint","IMPRINT",FACE,{"disambiguationData":[TD([[makeQuery(id+"F59.imprint","IMPRINT",EDGE,{"derivedFrom":sQuery(id+"F59.wireOp",EDGE,"E77")}),-1.0]])]});
            extrude(context, id + "F60", {"entities" : qUnion([Q0]), "operationType" : NewBodyOperationType.ADD, "oppositeDirection" : true, "depth" : 30 * mm, "offsetDistance" : 25 * mm});
        }
        {
            var Q0;
            Q0=makeQuery(id+"F9.boolean.opBoolean","MERGE",FACE,{"derivedFrom":[makeQuery(id+"F7.boolean.opBoolean","MERGE",FACE,{"derivedFrom":[makeQuery(id+"F5.boolean.opBoolean","MERGE",FACE,{"derivedFrom":[makeQuery(id+"F1.opExtrude","SWEPT_FACE",FACE,{"disambiguationData":[OSD([sQuery(id+"F0.wireOp",EDGE,"E0.left")])]}),makeQuery(id+"F5.opExtrude","SWEPT_FACE",FACE,{"disambiguationData":[OSD([sQuery(id+"F4.wireOp",EDGE,"E4.left")])]}),makeQuery(id+"F5.opExtrude","SWEPT_FACE",FACE,{"disambiguationData":[OSD([sQuery(id+"F4.wireOp",EDGE,"E5.right")])]}),makeQuery(id+"F5.opExtrude","SWEPT_FACE",FACE,{"disambiguationData":[OSD([sQuery(id+"F4.wireOp",EDGE,"E6.left")])]})]}),makeQuery(id+"F7.opExtrude","SWEPT_FACE",FACE,{"disambiguationData":[OSD([sQuery(id+"F6.wireOp",EDGE,"E7.right")])]})]}),makeQuery(id+"F9.opExtrude","CAP_FACE",FACE,{"disambiguationData":[OSD([sQuery(id+"F8.wireOp",EDGE,"E8"),sQuery(id+"F8.wireOp",EDGE,"E9"),sQuery(id+"F8.wireOp",EDGE,"E10"),sQuery(id+"F8.wireOp",EDGE,"E11")])],"isStart":true})]});
            var sketch = newSketch(context, id + "F61", { "sketchPlane" : qUnion([Q0])});
            skLineSegment(sketch, "E85", {"start": v(260, 170) * mm, "end": v(110, 170) * mm});
            skLineSegment(sketch, "E86", {"start": v(0, 30) * mm, "end": v(30, 30) * mm});
            skLineSegment(sketch, "E87", {"start": v(30, 30) * mm, "end": v(30, 47.57) * mm});
            skLineSegment(sketch, "E88", {"start": v(122.43, 140) * mm, "end": v(260, 140) * mm});
            skLineSegment(sketch, "E89", {"start": v(260, 140) * mm, "end": v(260, 170) * mm});
            skLineSegment(sketch, "E90", {"start": v(0, 30) * mm, "end": v(0, 60) * mm});
            skLineSegment(sketch, "E91", {"start": v(0, 60) * mm, "end": v(110, 170) * mm});
            skLineSegment(sketch, "E92", {"start": v(30, 47.57) * mm, "end": v(122.43, 140) * mm});
            skSolve(sketch);
        }
        {
            var Q0;
            Q0=makeQuery(id+"F61.imprint","IMPRINT",FACE,{"disambiguationData":[TD([[makeQuery(id+"F61.imprint","IMPRINT",EDGE,{"derivedFrom":sQuery(id+"F61.wireOp",EDGE,"E85")}),1.0]])]});
            extrude(context, id + "F62", {"entities" : qUnion([Q0]), "operationType" : NewBodyOperationType.ADD, "oppositeDirection" : true, "depth" : 30 * mm, "offsetDistance" : 25 * mm});
        }
        {
            var Q0;
            Q0=makeQuery(id+"F60.opExtrude","CAP_FACE",FACE,{"disambiguationData":[OSD([sQuery(id+"F59.wireOp",EDGE,"E77"),sQuery(id+"F59.wireOp",EDGE,"E78"),sQuery(id+"F59.wireOp",EDGE,"E79"),sQuery(id+"F59.wireOp",EDGE,"E80"),sQuery(id+"F59.wireOp",EDGE,"E81"),sQuery(id+"F59.wireOp",EDGE,"E82"),sQuery(id+"F59.wireOp",EDGE,"E83"),sQuery(id+"F59.wireOp",EDGE,"E84")])],"isStart":false});
            var sketch = newSketch(context, id + "F63", { "sketchPlane" : qUnion([Q0])});
            skCircle(sketch, "E93", {"center": v(60.68, 99.46) * mm, "radius": 15 * mm});
            skSolve(sketch);
        }
        {
            var Q0;
            {var subQ0=sQuery(id+"F63.wireOp",EDGE,"E93");var subQ1=makeQuery(id+"F63.imprint","INTERSECT",VERTEX,{"derivedFrom":[makeQuery(id+"F60.opExtrude","CAP_EDGE",EDGE,{"disambiguationData":[OSD([sQuery(id+"F59.wireOp",EDGE,"E83")])],"isStart":false}),subQ0]});Q0=makeQuery(id+"F63.imprint","IMPRINT",FACE,{"disambiguationData":[TD([[makeQuery(id+"F63.imprint","IMPRINT",EDGE,{"disambiguationData":[TD([[subQ1,1.0]])],"derivedFrom":subQ0}),1.0]])]});}
            extrude(context, id + "F64", {"entities" : qUnion([Q0]), "operationType" : NewBodyOperationType.ADD, "endBound" : BoundingType.UP_TO_NEXT, "depth" : 25 * mm, "offsetDistance" : 25 * mm});
        }
    });
